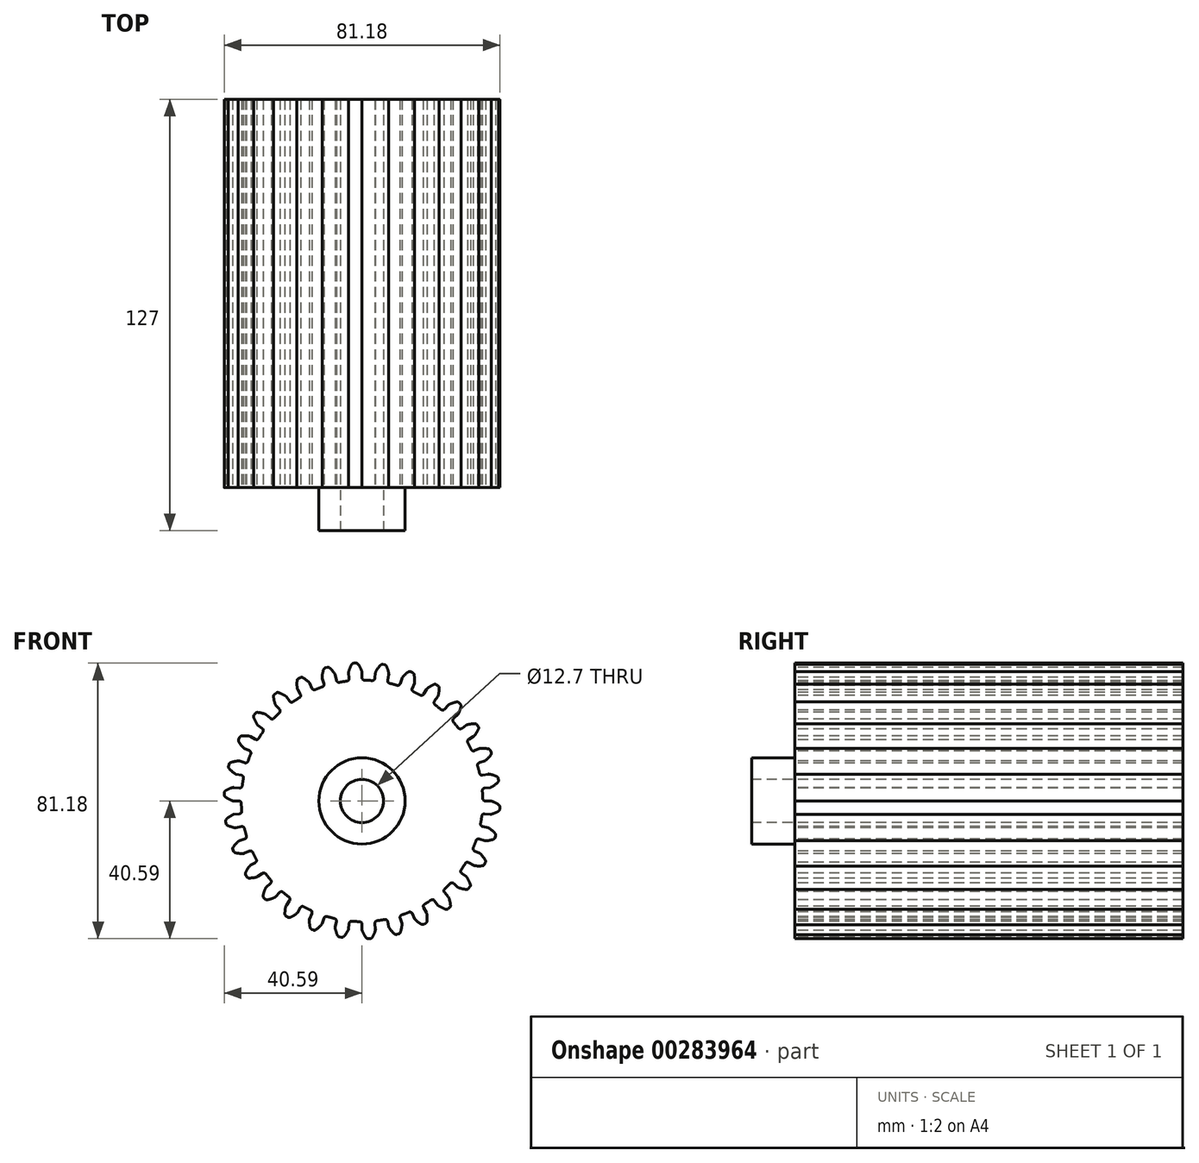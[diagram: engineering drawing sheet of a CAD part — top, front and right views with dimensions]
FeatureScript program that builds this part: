
annotation { "Feature Type Name" : "Feature", "Feature Type Description" : "" }
export const myFeature = defineFeature(function(context is Context, id is Id, definition is map)
    precondition{}
    {
        {
            var Q0;
            Q0=qCreatedBy(makeId("Front.planeOp"),FACE);
            var sketch = newSketch(context, id + "F0", { "sketchPlane" : qUnion([Q0])});
            skCircle(sketch, "E0", {"center": v(0, 0) * mm, "radius": 35.56 * mm});
            skSolve(sketch);
        }
        {
            var Q0;
            Q0 = qSketchRegion(id + "F0", true);
            extrude(context, id + "F1", {"entities" : qUnion([Q0]), "depth" : 57.15 * mm});
        }
        {
            var Q0;
            Q0=makeQuery(id+"F1.opExtrude","CAP_FACE",FACE,{"disambiguationData":[OSD([sQuery(id+"F0.wireOp",EDGE,"E0")])],"isStart":true});
            extrude(context, id + "F2", {"entities" : qUnion([Q0]), "operationType" : NewBodyOperationType.ADD, "depth" : 57.15 * mm});
        }
        {
            var Q0;
            Q0=makeQuery(id+"F1.opExtrude","CAP_FACE",FACE,{"disambiguationData":[OSD([sQuery(id+"F0.wireOp",EDGE,"E0")])],"isStart":false});
            var sketch = newSketch(context, id + "F3", { "sketchPlane" : qUnion([Q0])});
            skArc(sketch, "E1.trimOffspring", {"start": v(-0.06, 38.24) * mm, "mid": v(-0.56, 39.3) * mm, "end": v(-1.18, 40.28) * mm});
            skLineSegment(sketch, "E2", {"start": v(-1.84, 40.6) * mm, "end": v(-2.13, 40.58) * mm});
            skLineSegment(sketch, "E3", {"start": v(0, 37.96) * mm, "end": v(0, 36.31) * mm});
            skLineSegment(sketch, "E4.MirrorCS", {"start": v(-2.41, 40.56) * mm, "end": v(-2.13, 40.58) * mm});
            skArc(sketch, "E5.MirrorCS", {"start": v(-3.94, 38.04) * mm, "mid": v(-3.55, 39.14) * mm, "end": v(-3.03, 40.18) * mm});
            skPoint(sketch, "E6.visualSharp", {"position": v(-3.76, 35.36) * mm});
            skPoint(sketch, "E7.visualSharp", {"position": v(0, 35.56) * mm});
            skArc(sketch, "E7.filletArc", {"start": v(0, 36.31) * mm, "mid": v(0.22, 35.78) * mm, "end": v(0.75, 35.55) * mm});
            skArc(sketch, "E8", {"start": v(0.75, 35.55) * mm, "mid": v(-1.88, 35.51) * mm, "end": v(-4.5, 35.27) * mm});
            skLineSegment(sketch, "E9.MirrorCS", {"start": v(-3.97, 37.75) * mm, "end": v(-3.8, 36.12) * mm});
            skArc(sketch, "E10.MirrorCS", {"start": v(-3.8, 36.12) * mm, "mid": v(-3.96, 35.56) * mm, "end": v(-4.46, 35.28) * mm});
            skPoint(sketch, "E11.visualSharp", {"position": v(-3.98, 37.9) * mm});
            skArc(sketch, "E11.filletArc", {"start": v(-3.94, 38.04) * mm, "mid": v(-3.97, 37.9) * mm, "end": v(-3.97, 37.75) * mm});
            skPoint(sketch, "E12.visualSharp", {"position": v(-2.81, 40.54) * mm});
            skArc(sketch, "E12.filletArc", {"start": v(-2.41, 40.56) * mm, "mid": v(-2.77, 40.45) * mm, "end": v(-3.03, 40.18) * mm});
            skPoint(sketch, "E13.visualSharp", {"position": v(-1.44, 40.61) * mm});
            skArc(sketch, "E13.filletArc", {"start": v(-1.18, 40.28) * mm, "mid": v(-1.47, 40.52) * mm, "end": v(-1.84, 40.6) * mm});
            skPoint(sketch, "E14.visualSharp", {"position": v(0, 38.1) * mm});
            skArc(sketch, "E14.filletArc", {"start": v(0, 37.96) * mm, "mid": v(-0.01, 38.1) * mm, "end": v(-0.06, 38.24) * mm});
            skPoint(sketch, "E15.1.0", {"position": v(-11.77, 36.24) * mm});
            skArc(sketch, "E15.1.1", {"start": v(-6.66, 34.93) * mm, "mid": v(-9.22, 34.34) * mm, "end": v(-11.73, 33.57) * mm});
            skLineSegment(sketch, "E15.1.2", {"start": v(-11.73, 36.1) * mm, "end": v(-11.22, 34.54) * mm});
            skArc(sketch, "E15.1.3", {"start": v(-7.55, 35.52) * mm, "mid": v(-7.23, 35.04) * mm, "end": v(-6.66, 34.93) * mm});
            skPoint(sketch, "E15.1.4", {"position": v(-7.92, 37.27) * mm});
            skPoint(sketch, "E15.1.5", {"position": v(-7.4, 34.78) * mm});
            skArc(sketch, "E15.1.6", {"start": v(-11.22, 34.54) * mm, "mid": v(-11.26, 33.96) * mm, "end": v(-11.7, 33.58) * mm});
            skArc(sketch, "E15.1.7", {"start": v(-11.76, 36.39) * mm, "mid": v(-11.61, 37.54) * mm, "end": v(-11.32, 38.68) * mm});
            skPoint(sketch, "E15.1.8", {"position": v(-11.18, 39.07) * mm});
            skArc(sketch, "E15.1.9", {"start": v(-8, 37.4) * mm, "mid": v(-8.72, 38.32) * mm, "end": v(-9.53, 39.15) * mm});
            skPoint(sketch, "E15.1.10", {"position": v(-9.85, 39.43) * mm});
            skPoint(sketch, "E15.1.11", {"position": v(-11.03, 33.8) * mm});
            skLineSegment(sketch, "E15.1.12", {"start": v(-7.9, 37.13) * mm, "end": v(-7.55, 35.52) * mm});
            skArc(sketch, "E15.1.13", {"start": v(-9.53, 39.15) * mm, "mid": v(-9.87, 39.33) * mm, "end": v(-10.24, 39.32) * mm});
            skArc(sketch, "E15.1.14", {"start": v(-10.8, 39.18) * mm, "mid": v(-11.12, 39) * mm, "end": v(-11.32, 38.68) * mm});
            skLineSegment(sketch, "E15.1.15", {"start": v(-10.8, 39.18) * mm, "end": v(-10.52, 39.25) * mm});
            skLineSegment(sketch, "E15.1.16", {"start": v(-10.24, 39.32) * mm, "end": v(-10.52, 39.25) * mm});
            skArc(sketch, "E15.1.17", {"start": v(-11.76, 36.39) * mm, "mid": v(-11.76, 36.24) * mm, "end": v(-11.73, 36.1) * mm});
            skArc(sketch, "E15.1.18", {"start": v(-7.9, 37.13) * mm, "mid": v(-7.94, 37.27) * mm, "end": v(-8, 37.4) * mm});
            skPoint(sketch, "E15.2.0", {"position": v(-19.05, 33) * mm});
            skArc(sketch, "E15.2.1", {"start": v(-13.78, 32.78) * mm, "mid": v(-16.16, 31.67) * mm, "end": v(-18.46, 30.4) * mm});
            skLineSegment(sketch, "E15.2.2", {"start": v(-18.98, 32.87) * mm, "end": v(-18.16, 31.45) * mm});
            skArc(sketch, "E15.2.3", {"start": v(-14.77, 33.17) * mm, "mid": v(-14.35, 32.78) * mm, "end": v(-13.78, 32.78) * mm});
            skPoint(sketch, "E15.2.4", {"position": v(-15.5, 34.8) * mm});
            skPoint(sketch, "E15.2.5", {"position": v(-14.46, 32.49) * mm});
            skArc(sketch, "E15.2.6", {"start": v(-18.16, 31.45) * mm, "mid": v(-18.08, 30.88) * mm, "end": v(-18.42, 30.42) * mm});
            skArc(sketch, "E15.2.7", {"start": v(-19.07, 33.14) * mm, "mid": v(-19.16, 34.3) * mm, "end": v(-19.11, 35.48) * mm});
            skPoint(sketch, "E15.2.8", {"position": v(-19.06, 35.9) * mm});
            skArc(sketch, "E15.2.9", {"start": v(-15.6, 34.91) * mm, "mid": v(-16.5, 35.67) * mm, "end": v(-17.47, 36.32) * mm});
            skPoint(sketch, "E15.2.10", {"position": v(-17.83, 36.52) * mm});
            skPoint(sketch, "E15.2.11", {"position": v(-17.82, 30.77) * mm});
            skLineSegment(sketch, "E15.2.12", {"start": v(-15.44, 34.67) * mm, "end": v(-14.77, 33.17) * mm});
            skArc(sketch, "E15.2.13", {"start": v(-17.47, 36.32) * mm, "mid": v(-17.83, 36.42) * mm, "end": v(-18.2, 36.34) * mm});
            skArc(sketch, "E15.2.14", {"start": v(-18.7, 36.08) * mm, "mid": v(-18.98, 35.83) * mm, "end": v(-19.11, 35.48) * mm});
            skLineSegment(sketch, "E15.2.15", {"start": v(-18.7, 36.08) * mm, "end": v(-18.45, 36.2) * mm});
            skLineSegment(sketch, "E15.2.16", {"start": v(-18.2, 36.34) * mm, "end": v(-18.45, 36.2) * mm});
            skArc(sketch, "E15.2.17", {"start": v(-19.07, 33.14) * mm, "mid": v(-19.04, 33) * mm, "end": v(-18.98, 32.87) * mm});
            skArc(sketch, "E15.2.18", {"start": v(-15.44, 34.67) * mm, "mid": v(-15.5, 34.8) * mm, "end": v(-15.6, 34.91) * mm});
            skArc(sketch, "E16.1.3.0", {"start": v(-20.3, 29.2) * mm, "mid": v(-22.4, 27.62) * mm, "end": v(-24.37, 25.9) * mm});
            skLineSegment(sketch, "E16.5.3.0", {"start": v(-25.4, 28.2) * mm, "end": v(-24.3, 26.99) * mm});
            skArc(sketch, "E16.8.3.0", {"start": v(-21.34, 29.38) * mm, "mid": v(-20.86, 29.08) * mm, "end": v(-20.3, 29.2) * mm});
            skPoint(sketch, "E16.12.3.0", {"position": v(-22.4, 30.82) * mm});
            skPoint(sketch, "E16.13.3.0", {"position": v(-20.9, 28.77) * mm});
            skArc(sketch, "E16.14.3.0", {"start": v(-24.3, 26.99) * mm, "mid": v(-24.1, 26.44) * mm, "end": v(-24.34, 25.92) * mm});
            skArc(sketch, "E16.18.3.0", {"start": v(-25.55, 28.45) * mm, "mid": v(-25.88, 29.57) * mm, "end": v(-26.07, 30.73) * mm});
            skPoint(sketch, "E16.22.3.0", {"position": v(-26.1, 31.15) * mm});
            skArc(sketch, "E16.23.3.0", {"start": v(-22.52, 30.9) * mm, "mid": v(-23.55, 31.46) * mm, "end": v(-24.63, 31.9) * mm});
            skPoint(sketch, "E16.24.3.0", {"position": v(-25.5, 28.31) * mm});
            skPoint(sketch, "E16.27.3.0", {"position": v(-25.04, 32.01) * mm});
            skPoint(sketch, "E16.28.3.0", {"position": v(-23.83, 26.4) * mm});
            skLineSegment(sketch, "E16.29.3.0", {"start": v(-22.3, 30.7) * mm, "end": v(-21.34, 29.38) * mm});
            skArc(sketch, "E16.32.3.0", {"start": v(-24.63, 31.9) * mm, "mid": v(-25, 31.92) * mm, "end": v(-25.35, 31.76) * mm});
            skArc(sketch, "E16.36.3.0", {"start": v(-25.8, 31.4) * mm, "mid": v(-26.02, 31.1) * mm, "end": v(-26.07, 30.73) * mm});
            skLineSegment(sketch, "E16.40.3.0", {"start": v(-25.8, 31.4) * mm, "end": v(-25.57, 31.58) * mm});
            skLineSegment(sketch, "E16.43.3.0", {"start": v(-25.35, 31.76) * mm, "end": v(-25.57, 31.58) * mm});
            skArc(sketch, "E16.46.3.0", {"start": v(-25.55, 28.45) * mm, "mid": v(-25.48, 28.32) * mm, "end": v(-25.4, 28.2) * mm});
            skArc(sketch, "E16.50.3.0", {"start": v(-22.3, 30.7) * mm, "mid": v(-22.4, 30.82) * mm, "end": v(-22.52, 30.9) * mm});
            skArc(sketch, "E16.1.4.0", {"start": v(-25.92, 24.34) * mm, "mid": v(-27.65, 22.36) * mm, "end": v(-29.22, 20.26) * mm});
            skLineSegment(sketch, "E16.5.4.0", {"start": v(-30.7, 22.3) * mm, "end": v(-29.38, 21.34) * mm});
            skArc(sketch, "E16.8.4.0", {"start": v(-26.99, 24.3) * mm, "mid": v(-26.44, 24.1) * mm, "end": v(-25.92, 24.34) * mm});
            skPoint(sketch, "E16.12.4.0", {"position": v(-28.31, 25.5) * mm});
            skPoint(sketch, "E16.13.4.0", {"position": v(-26.43, 23.8) * mm});
            skArc(sketch, "E16.14.4.0", {"start": v(-29.38, 21.34) * mm, "mid": v(-29.08, 20.86) * mm, "end": v(-29.2, 20.3) * mm});
            skArc(sketch, "E16.18.4.0", {"start": v(-30.9, 22.52) * mm, "mid": v(-31.46, 23.55) * mm, "end": v(-31.9, 24.63) * mm});
            skPoint(sketch, "E16.22.4.0", {"position": v(-32.01, 25.04) * mm});
            skArc(sketch, "E16.23.4.0", {"start": v(-28.45, 25.55) * mm, "mid": v(-29.57, 25.88) * mm, "end": v(-30.73, 26.07) * mm});
            skPoint(sketch, "E16.24.4.0", {"position": v(-30.82, 22.4) * mm});
            skPoint(sketch, "E16.27.4.0", {"position": v(-31.15, 26.1) * mm});
            skPoint(sketch, "E16.28.4.0", {"position": v(-28.8, 20.87) * mm});
            skLineSegment(sketch, "E16.29.4.0", {"start": v(-28.2, 25.4) * mm, "end": v(-26.99, 24.3) * mm});
            skArc(sketch, "E16.32.4.0", {"start": v(-30.73, 26.07) * mm, "mid": v(-31.1, 26.02) * mm, "end": v(-31.4, 25.8) * mm});
            skArc(sketch, "E16.36.4.0", {"start": v(-31.76, 25.35) * mm, "mid": v(-31.92, 25) * mm, "end": v(-31.9, 24.63) * mm});
            skLineSegment(sketch, "E16.40.4.0", {"start": v(-31.76, 25.35) * mm, "end": v(-31.58, 25.57) * mm});
            skLineSegment(sketch, "E16.43.4.0", {"start": v(-31.4, 25.8) * mm, "end": v(-31.58, 25.57) * mm});
            skArc(sketch, "E16.46.4.0", {"start": v(-30.9, 22.52) * mm, "mid": v(-30.82, 22.4) * mm, "end": v(-30.7, 22.3) * mm});
            skArc(sketch, "E16.50.4.0", {"start": v(-28.2, 25.4) * mm, "mid": v(-28.32, 25.48) * mm, "end": v(-28.45, 25.55) * mm});
            skArc(sketch, "E16.1.5.0", {"start": v(-30.42, 18.42) * mm, "mid": v(-31.7, 16.13) * mm, "end": v(-32.8, 13.74) * mm});
            skLineSegment(sketch, "E16.5.5.0", {"start": v(-34.67, 15.44) * mm, "end": v(-33.17, 14.77) * mm});
            skArc(sketch, "E16.8.5.0", {"start": v(-31.45, 18.16) * mm, "mid": v(-30.88, 18.08) * mm, "end": v(-30.42, 18.42) * mm});
            skPoint(sketch, "E16.12.5.0", {"position": v(-33, 19.05) * mm});
            skPoint(sketch, "E16.13.5.0", {"position": v(-30.8, 17.78) * mm});
            skArc(sketch, "E16.14.5.0", {"start": v(-33.17, 14.77) * mm, "mid": v(-32.78, 14.35) * mm, "end": v(-32.78, 13.78) * mm});
            skArc(sketch, "E16.18.5.0", {"start": v(-34.91, 15.6) * mm, "mid": v(-35.67, 16.5) * mm, "end": v(-36.32, 17.47) * mm});
            skPoint(sketch, "E16.22.5.0", {"position": v(-36.52, 17.83) * mm});
            skArc(sketch, "E16.23.5.0", {"start": v(-33.14, 19.07) * mm, "mid": v(-34.3, 19.16) * mm, "end": v(-35.48, 19.11) * mm});
            skPoint(sketch, "E16.24.5.0", {"position": v(-34.8, 15.5) * mm});
            skPoint(sketch, "E16.27.5.0", {"position": v(-35.9, 19.06) * mm});
            skPoint(sketch, "E16.28.5.0", {"position": v(-32.5, 14.42) * mm});
            skLineSegment(sketch, "E16.29.5.0", {"start": v(-32.87, 18.98) * mm, "end": v(-31.45, 18.16) * mm});
            skArc(sketch, "E16.32.5.0", {"start": v(-35.48, 19.11) * mm, "mid": v(-35.83, 18.98) * mm, "end": v(-36.08, 18.7) * mm});
            skArc(sketch, "E16.36.5.0", {"start": v(-36.34, 18.2) * mm, "mid": v(-36.42, 17.83) * mm, "end": v(-36.32, 17.47) * mm});
            skLineSegment(sketch, "E16.40.5.0", {"start": v(-36.34, 18.2) * mm, "end": v(-36.2, 18.45) * mm});
            skLineSegment(sketch, "E16.43.5.0", {"start": v(-36.08, 18.7) * mm, "end": v(-36.2, 18.45) * mm});
            skArc(sketch, "E16.46.5.0", {"start": v(-34.91, 15.6) * mm, "mid": v(-34.8, 15.5) * mm, "end": v(-34.67, 15.44) * mm});
            skArc(sketch, "E16.50.5.0", {"start": v(-32.87, 18.98) * mm, "mid": v(-33, 19.04) * mm, "end": v(-33.14, 19.07) * mm});
            skArc(sketch, "E16.1.6.0", {"start": v(-33.58, 11.7) * mm, "mid": v(-34.35, 9.18) * mm, "end": v(-34.94, 6.62) * mm});
            skLineSegment(sketch, "E16.5.6.0", {"start": v(-37.13, 7.9) * mm, "end": v(-35.52, 7.55) * mm});
            skArc(sketch, "E16.8.6.0", {"start": v(-34.54, 11.22) * mm, "mid": v(-33.96, 11.26) * mm, "end": v(-33.58, 11.7) * mm});
            skPoint(sketch, "E16.12.6.0", {"position": v(-36.24, 11.77) * mm});
            skPoint(sketch, "E16.13.6.0", {"position": v(-33.82, 10.99) * mm});
            skArc(sketch, "E16.14.6.0", {"start": v(-35.52, 7.55) * mm, "mid": v(-35.04, 7.23) * mm, "end": v(-34.93, 6.66) * mm});
            skArc(sketch, "E16.18.6.0", {"start": v(-37.4, 8) * mm, "mid": v(-38.32, 8.72) * mm, "end": v(-39.15, 9.53) * mm});
            skPoint(sketch, "E16.22.6.0", {"position": v(-39.43, 9.85) * mm});
            skArc(sketch, "E16.23.6.0", {"start": v(-36.39, 11.76) * mm, "mid": v(-37.54, 11.61) * mm, "end": v(-38.68, 11.32) * mm});
            skPoint(sketch, "E16.24.6.0", {"position": v(-37.27, 7.92) * mm});
            skPoint(sketch, "E16.27.6.0", {"position": v(-39.07, 11.18) * mm});
            skPoint(sketch, "E16.28.6.0", {"position": v(-34.8, 7.35) * mm});
            skLineSegment(sketch, "E16.29.6.0", {"start": v(-36.1, 11.73) * mm, "end": v(-34.54, 11.22) * mm});
            skArc(sketch, "E16.32.6.0", {"start": v(-38.68, 11.32) * mm, "mid": v(-39, 11.12) * mm, "end": v(-39.18, 10.8) * mm});
            skArc(sketch, "E16.36.6.0", {"start": v(-39.32, 10.24) * mm, "mid": v(-39.33, 9.87) * mm, "end": v(-39.15, 9.53) * mm});
            skLineSegment(sketch, "E16.40.6.0", {"start": v(-39.32, 10.24) * mm, "end": v(-39.25, 10.52) * mm});
            skLineSegment(sketch, "E16.43.6.0", {"start": v(-39.18, 10.8) * mm, "end": v(-39.25, 10.52) * mm});
            skArc(sketch, "E16.46.6.0", {"start": v(-37.4, 8) * mm, "mid": v(-37.27, 7.94) * mm, "end": v(-37.13, 7.9) * mm});
            skArc(sketch, "E16.50.6.0", {"start": v(-36.1, 11.73) * mm, "mid": v(-36.24, 11.76) * mm, "end": v(-36.39, 11.76) * mm});
            skArc(sketch, "E16.1.7.0", {"start": v(-35.28, 4.46) * mm, "mid": v(-35.51, 1.84) * mm, "end": v(-35.55, -0.79) * mm});
            skLineSegment(sketch, "E16.5.7.0", {"start": v(-37.96, 0) * mm, "end": v(-36.31, 0) * mm});
            skArc(sketch, "E16.8.7.0", {"start": v(-36.12, 3.8) * mm, "mid": v(-35.56, 3.96) * mm, "end": v(-35.28, 4.46) * mm});
            skPoint(sketch, "E16.12.7.0", {"position": v(-37.9, 3.98) * mm});
            skPoint(sketch, "E16.13.7.0", {"position": v(-35.37, 3.72) * mm});
            skArc(sketch, "E16.14.7.0", {"start": v(-36.31, 0) * mm, "mid": v(-35.78, -0.22) * mm, "end": v(-35.55, -0.75) * mm});
            skArc(sketch, "E16.18.7.0", {"start": v(-38.24, 0.06) * mm, "mid": v(-39.3, 0.56) * mm, "end": v(-40.28, 1.18) * mm});
            skPoint(sketch, "E16.22.7.0", {"position": v(-40.61, 1.44) * mm});
            skArc(sketch, "E16.23.7.0", {"start": v(-38.04, 3.94) * mm, "mid": v(-39.14, 3.55) * mm, "end": v(-40.18, 3.03) * mm});
            skPoint(sketch, "E16.24.7.0", {"position": v(-38.1, 0) * mm});
            skPoint(sketch, "E16.27.7.0", {"position": v(-40.54, 2.81) * mm});
            skPoint(sketch, "E16.28.7.0", {"position": v(-35.56, -0.04) * mm});
            skLineSegment(sketch, "E16.29.7.0", {"start": v(-37.75, 3.97) * mm, "end": v(-36.12, 3.8) * mm});
            skArc(sketch, "E16.32.7.0", {"start": v(-40.18, 3.03) * mm, "mid": v(-40.45, 2.77) * mm, "end": v(-40.56, 2.41) * mm});
            skArc(sketch, "E16.36.7.0", {"start": v(-40.6, 1.84) * mm, "mid": v(-40.52, 1.47) * mm, "end": v(-40.28, 1.18) * mm});
            skLineSegment(sketch, "E16.40.7.0", {"start": v(-40.6, 1.84) * mm, "end": v(-40.58, 2.13) * mm});
            skLineSegment(sketch, "E16.43.7.0", {"start": v(-40.56, 2.41) * mm, "end": v(-40.58, 2.13) * mm});
            skArc(sketch, "E16.46.7.0", {"start": v(-38.24, 0.06) * mm, "mid": v(-38.1, 0.01) * mm, "end": v(-37.96, 0) * mm});
            skArc(sketch, "E16.50.7.0", {"start": v(-37.75, 3.97) * mm, "mid": v(-37.9, 3.97) * mm, "end": v(-38.04, 3.94) * mm});
            skArc(sketch, "E16.1.8.0", {"start": v(-35.44, -2.97) * mm, "mid": v(-35.12, -5.58) * mm, "end": v(-34.61, -8.16) * mm});
            skLineSegment(sketch, "E16.5.8.0", {"start": v(-37.13, -7.9) * mm, "end": v(-35.52, -7.55) * mm});
            skArc(sketch, "E16.8.8.0", {"start": v(-36.12, -3.8) * mm, "mid": v(-35.6, -3.52) * mm, "end": v(-35.44, -2.97) * mm});
            skPoint(sketch, "E16.12.8.0", {"position": v(-37.9, -3.98) * mm});
            skPoint(sketch, "E16.13.8.0", {"position": v(-35.37, -3.72) * mm});
            skArc(sketch, "E16.14.8.0", {"start": v(-35.52, -7.55) * mm, "mid": v(-34.95, -7.65) * mm, "end": v(-34.62, -8.12) * mm});
            skArc(sketch, "E16.18.8.0", {"start": v(-37.42, -7.9) * mm, "mid": v(-38.55, -7.62) * mm, "end": v(-39.65, -7.22) * mm});
            skPoint(sketch, "E16.22.8.0", {"position": v(-40.03, -7.04) * mm});
            skArc(sketch, "E16.23.8.0", {"start": v(-38.02, -4.05) * mm, "mid": v(-39.02, -4.66) * mm, "end": v(-39.94, -5.39) * mm});
            skPoint(sketch, "E16.24.8.0", {"position": v(-37.27, -7.92) * mm});
            skPoint(sketch, "E16.27.8.0", {"position": v(-40.24, -5.68) * mm});
            skPoint(sketch, "E16.28.8.0", {"position": v(-34.77, -7.43) * mm});
            skLineSegment(sketch, "E16.29.8.0", {"start": v(-37.75, -3.97) * mm, "end": v(-36.12, -3.8) * mm});
            skArc(sketch, "E16.32.8.0", {"start": v(-39.94, -5.39) * mm, "mid": v(-40.14, -5.7) * mm, "end": v(-40.18, -6.07) * mm});
            skArc(sketch, "E16.36.8.0", {"start": v(-40.09, -6.64) * mm, "mid": v(-39.94, -6.98) * mm, "end": v(-39.65, -7.22) * mm});
            skLineSegment(sketch, "E16.40.8.0", {"start": v(-40.09, -6.64) * mm, "end": v(-40.13, -6.36) * mm});
            skLineSegment(sketch, "E16.43.8.0", {"start": v(-40.18, -6.07) * mm, "end": v(-40.13, -6.36) * mm});
            skArc(sketch, "E16.46.8.0", {"start": v(-37.42, -7.9) * mm, "mid": v(-37.27, -7.9) * mm, "end": v(-37.13, -7.9) * mm});
            skArc(sketch, "E16.50.8.0", {"start": v(-37.75, -3.97) * mm, "mid": v(-37.9, -4) * mm, "end": v(-38.02, -4.05) * mm});
            skArc(sketch, "E16.1.9.0", {"start": v(-34.04, -10.28) * mm, "mid": v(-33.2, -12.76) * mm, "end": v(-32.16, -15.18) * mm});
            skLineSegment(sketch, "E16.5.9.0", {"start": v(-34.67, -15.44) * mm, "end": v(-33.17, -14.77) * mm});
            skArc(sketch, "E16.8.9.0", {"start": v(-34.54, -11.22) * mm, "mid": v(-34.1, -10.85) * mm, "end": v(-34.04, -10.28) * mm});
            skPoint(sketch, "E16.12.9.0", {"position": v(-36.24, -11.77) * mm});
            skPoint(sketch, "E16.13.9.0", {"position": v(-33.82, -10.99) * mm});
            skArc(sketch, "E16.14.9.0", {"start": v(-33.17, -14.77) * mm, "mid": v(-32.6, -14.75) * mm, "end": v(-32.18, -15.14) * mm});
            skArc(sketch, "E16.18.9.0", {"start": v(-34.96, -15.5) * mm, "mid": v(-36.12, -15.47) * mm, "end": v(-37.28, -15.3) * mm});
            skPoint(sketch, "E16.22.9.0", {"position": v(-37.69, -15.2) * mm});
            skArc(sketch, "E16.23.9.0", {"start": v(-36.35, -11.87) * mm, "mid": v(-37.2, -12.67) * mm, "end": v(-37.94, -13.57) * mm});
            skPoint(sketch, "E16.24.9.0", {"position": v(-34.8, -15.5) * mm});
            skPoint(sketch, "E16.27.9.0", {"position": v(-38.18, -13.92) * mm});
            skPoint(sketch, "E16.28.9.0", {"position": v(-32.47, -14.5) * mm});
            skLineSegment(sketch, "E16.29.9.0", {"start": v(-36.1, -11.73) * mm, "end": v(-34.54, -11.22) * mm});
            skArc(sketch, "E16.32.9.0", {"start": v(-37.94, -13.57) * mm, "mid": v(-38.08, -13.92) * mm, "end": v(-38.04, -14.3) * mm});
            skArc(sketch, "E16.36.9.0", {"start": v(-37.83, -14.83) * mm, "mid": v(-37.62, -15.14) * mm, "end": v(-37.28, -15.3) * mm});
            skLineSegment(sketch, "E16.40.9.0", {"start": v(-37.83, -14.83) * mm, "end": v(-37.94, -14.56) * mm});
            skLineSegment(sketch, "E16.43.9.0", {"start": v(-38.04, -14.3) * mm, "end": v(-37.94, -14.56) * mm});
            skArc(sketch, "E16.46.9.0", {"start": v(-34.96, -15.5) * mm, "mid": v(-34.81, -15.48) * mm, "end": v(-34.67, -15.44) * mm});
            skArc(sketch, "E16.50.9.0", {"start": v(-36.1, -11.73) * mm, "mid": v(-36.23, -11.79) * mm, "end": v(-36.35, -11.87) * mm});
            skArc(sketch, "E16.1.10.0", {"start": v(-31.16, -17.13) * mm, "mid": v(-29.81, -19.38) * mm, "end": v(-28.3, -21.53) * mm});
            skLineSegment(sketch, "E16.5.10.0", {"start": v(-30.7, -22.3) * mm, "end": v(-29.38, -21.34) * mm});
            skArc(sketch, "E16.8.10.0", {"start": v(-31.45, -18.16) * mm, "mid": v(-31.1, -17.7) * mm, "end": v(-31.16, -17.13) * mm});
            skPoint(sketch, "E16.12.10.0", {"position": v(-33, -19.05) * mm});
            skPoint(sketch, "E16.13.10.0", {"position": v(-30.8, -17.78) * mm});
            skArc(sketch, "E16.14.10.0", {"start": v(-29.38, -21.34) * mm, "mid": v(-28.82, -21.2) * mm, "end": v(-28.32, -21.5) * mm});
            skArc(sketch, "E16.18.10.0", {"start": v(-30.97, -22.43) * mm, "mid": v(-32.12, -22.65) * mm, "end": v(-33.28, -22.72) * mm});
            skPoint(sketch, "E16.22.10.0", {"position": v(-33.7, -22.7) * mm});
            skArc(sketch, "E16.23.10.0", {"start": v(-33.09, -19.17) * mm, "mid": v(-33.75, -20.13) * mm, "end": v(-34.3, -21.17) * mm});
            skPoint(sketch, "E16.24.10.0", {"position": v(-30.82, -22.4) * mm});
            skPoint(sketch, "E16.27.10.0", {"position": v(-34.45, -21.55) * mm});
            skPoint(sketch, "E16.28.10.0", {"position": v(-28.74, -20.94) * mm});
            skLineSegment(sketch, "E16.29.10.0", {"start": v(-32.87, -18.98) * mm, "end": v(-31.45, -18.16) * mm});
            skArc(sketch, "E16.32.10.0", {"start": v(-34.3, -21.17) * mm, "mid": v(-34.35, -21.54) * mm, "end": v(-34.23, -21.9) * mm});
            skArc(sketch, "E16.36.10.0", {"start": v(-33.92, -22.37) * mm, "mid": v(-33.65, -22.63) * mm, "end": v(-33.28, -22.72) * mm});
            skLineSegment(sketch, "E16.40.10.0", {"start": v(-33.92, -22.37) * mm, "end": v(-34.08, -22.13) * mm});
            skLineSegment(sketch, "E16.43.10.0", {"start": v(-34.23, -21.9) * mm, "end": v(-34.08, -22.13) * mm});
            skArc(sketch, "E16.46.10.0", {"start": v(-30.97, -22.43) * mm, "mid": v(-30.83, -22.38) * mm, "end": v(-30.7, -22.3) * mm});
            skArc(sketch, "E16.50.10.0", {"start": v(-32.87, -18.98) * mm, "mid": v(-32.99, -19.06) * mm, "end": v(-33.09, -19.17) * mm});
            skArc(sketch, "E16.1.11.0", {"start": v(-26.92, -23.23) * mm, "mid": v(-25.13, -25.16) * mm, "end": v(-23.2, -26.95) * mm});
            skLineSegment(sketch, "E16.5.11.0", {"start": v(-25.4, -28.2) * mm, "end": v(-24.3, -26.99) * mm});
            skArc(sketch, "E16.8.11.0", {"start": v(-26.99, -24.3) * mm, "mid": v(-26.74, -23.78) * mm, "end": v(-26.92, -23.23) * mm});
            skPoint(sketch, "E16.12.11.0", {"position": v(-28.31, -25.5) * mm});
            skPoint(sketch, "E16.13.11.0", {"position": v(-26.43, -23.8) * mm});
            skArc(sketch, "E16.14.11.0", {"start": v(-24.3, -26.99) * mm, "mid": v(-23.78, -26.74) * mm, "end": v(-23.23, -26.92) * mm});
            skArc(sketch, "E16.18.11.0", {"start": v(-25.63, -28.38) * mm, "mid": v(-26.7, -28.83) * mm, "end": v(-27.83, -29.14) * mm});
            skPoint(sketch, "E16.22.11.0", {"position": v(-28.25, -29.22) * mm});
            skArc(sketch, "E16.23.11.0", {"start": v(-28.38, -25.63) * mm, "mid": v(-28.83, -26.7) * mm, "end": v(-29.14, -27.83) * mm});
            skPoint(sketch, "E16.24.11.0", {"position": v(-25.5, -28.31) * mm});
            skPoint(sketch, "E16.27.11.0", {"position": v(-29.22, -28.25) * mm});
            skPoint(sketch, "E16.28.11.0", {"position": v(-23.76, -26.45) * mm});
            skLineSegment(sketch, "E16.29.11.0", {"start": v(-28.2, -25.4) * mm, "end": v(-26.99, -24.3) * mm});
            skArc(sketch, "E16.32.11.0", {"start": v(-29.14, -27.83) * mm, "mid": v(-29.13, -28.2) * mm, "end": v(-28.93, -28.53) * mm});
            skArc(sketch, "E16.36.11.0", {"start": v(-28.53, -28.93) * mm, "mid": v(-28.2, -29.13) * mm, "end": v(-27.83, -29.14) * mm});
            skLineSegment(sketch, "E16.40.11.0", {"start": v(-28.53, -28.93) * mm, "end": v(-28.73, -28.73) * mm});
            skLineSegment(sketch, "E16.43.11.0", {"start": v(-28.93, -28.53) * mm, "end": v(-28.73, -28.73) * mm});
            skArc(sketch, "E16.46.11.0", {"start": v(-25.63, -28.38) * mm, "mid": v(-25.5, -28.3) * mm, "end": v(-25.4, -28.2) * mm});
            skArc(sketch, "E16.50.11.0", {"start": v(-28.2, -25.4) * mm, "mid": v(-28.3, -25.5) * mm, "end": v(-28.38, -25.63) * mm});
            skArc(sketch, "E16.1.12.0", {"start": v(-21.5, -28.32) * mm, "mid": v(-19.35, -29.83) * mm, "end": v(-17.1, -31.18) * mm});
            skLineSegment(sketch, "E16.5.12.0", {"start": v(-18.98, -32.87) * mm, "end": v(-18.16, -31.45) * mm});
            skArc(sketch, "E16.8.12.0", {"start": v(-21.34, -29.38) * mm, "mid": v(-21.2, -28.82) * mm, "end": v(-21.5, -28.32) * mm});
            skPoint(sketch, "E16.12.12.0", {"position": v(-22.4, -30.82) * mm});
            skPoint(sketch, "E16.13.12.0", {"position": v(-20.9, -28.77) * mm});
            skArc(sketch, "E16.14.12.0", {"start": v(-18.16, -31.45) * mm, "mid": v(-17.7, -31.1) * mm, "end": v(-17.13, -31.16) * mm});
            skArc(sketch, "E16.18.12.0", {"start": v(-19.17, -33.09) * mm, "mid": v(-20.13, -33.75) * mm, "end": v(-21.17, -34.3) * mm});
            skPoint(sketch, "E16.22.12.0", {"position": v(-21.55, -34.45) * mm});
            skArc(sketch, "E16.23.12.0", {"start": v(-22.43, -30.97) * mm, "mid": v(-22.65, -32.12) * mm, "end": v(-22.72, -33.28) * mm});
            skPoint(sketch, "E16.24.12.0", {"position": v(-19.05, -33) * mm});
            skPoint(sketch, "E16.27.12.0", {"position": v(-22.7, -33.7) * mm});
            skPoint(sketch, "E16.28.12.0", {"position": v(-17.74, -30.82) * mm});
            skLineSegment(sketch, "E16.29.12.0", {"start": v(-22.3, -30.7) * mm, "end": v(-21.34, -29.38) * mm});
            skArc(sketch, "E16.32.12.0", {"start": v(-22.72, -33.28) * mm, "mid": v(-22.63, -33.65) * mm, "end": v(-22.37, -33.92) * mm});
            skArc(sketch, "E16.36.12.0", {"start": v(-21.9, -34.23) * mm, "mid": v(-21.54, -34.35) * mm, "end": v(-21.17, -34.3) * mm});
            skLineSegment(sketch, "E16.40.12.0", {"start": v(-21.9, -34.23) * mm, "end": v(-22.13, -34.08) * mm});
            skLineSegment(sketch, "E16.43.12.0", {"start": v(-22.37, -33.92) * mm, "end": v(-22.13, -34.08) * mm});
            skArc(sketch, "E16.46.12.0", {"start": v(-19.17, -33.09) * mm, "mid": v(-19.06, -32.99) * mm, "end": v(-18.98, -32.87) * mm});
            skArc(sketch, "E16.50.12.0", {"start": v(-22.3, -30.7) * mm, "mid": v(-22.38, -30.83) * mm, "end": v(-22.43, -30.97) * mm});
            skArc(sketch, "E16.1.13.0", {"start": v(-15.14, -32.18) * mm, "mid": v(-12.72, -33.2) * mm, "end": v(-10.24, -34.05) * mm});
            skLineSegment(sketch, "E16.5.13.0", {"start": v(-11.73, -36.1) * mm, "end": v(-11.22, -34.54) * mm});
            skArc(sketch, "E16.8.13.0", {"start": v(-14.77, -33.17) * mm, "mid": v(-14.75, -32.6) * mm, "end": v(-15.14, -32.18) * mm});
            skPoint(sketch, "E16.12.13.0", {"position": v(-15.5, -34.8) * mm});
            skPoint(sketch, "E16.13.13.0", {"position": v(-14.46, -32.49) * mm});
            skArc(sketch, "E16.14.13.0", {"start": v(-11.22, -34.54) * mm, "mid": v(-10.85, -34.1) * mm, "end": v(-10.28, -34.04) * mm});
            skArc(sketch, "E16.18.13.0", {"start": v(-11.87, -36.35) * mm, "mid": v(-12.67, -37.2) * mm, "end": v(-13.57, -37.94) * mm});
            skPoint(sketch, "E16.22.13.0", {"position": v(-13.92, -38.18) * mm});
            skArc(sketch, "E16.23.13.0", {"start": v(-15.5, -34.96) * mm, "mid": v(-15.47, -36.12) * mm, "end": v(-15.3, -37.28) * mm});
            skPoint(sketch, "E16.24.13.0", {"position": v(-11.77, -36.24) * mm});
            skPoint(sketch, "E16.27.13.0", {"position": v(-15.2, -37.69) * mm});
            skPoint(sketch, "E16.28.13.0", {"position": v(-10.95, -33.83) * mm});
            skLineSegment(sketch, "E16.29.13.0", {"start": v(-15.44, -34.67) * mm, "end": v(-14.77, -33.17) * mm});
            skArc(sketch, "E16.32.13.0", {"start": v(-15.3, -37.28) * mm, "mid": v(-15.14, -37.62) * mm, "end": v(-14.83, -37.83) * mm});
            skArc(sketch, "E16.36.13.0", {"start": v(-14.3, -38.04) * mm, "mid": v(-13.92, -38.08) * mm, "end": v(-13.57, -37.94) * mm});
            skLineSegment(sketch, "E16.40.13.0", {"start": v(-14.3, -38.04) * mm, "end": v(-14.56, -37.94) * mm});
            skLineSegment(sketch, "E16.43.13.0", {"start": v(-14.83, -37.83) * mm, "end": v(-14.56, -37.94) * mm});
            skArc(sketch, "E16.46.13.0", {"start": v(-11.87, -36.35) * mm, "mid": v(-11.79, -36.23) * mm, "end": v(-11.73, -36.1) * mm});
            skArc(sketch, "E16.50.13.0", {"start": v(-15.44, -34.67) * mm, "mid": v(-15.48, -34.81) * mm, "end": v(-15.5, -34.96) * mm});
            skArc(sketch, "E16.1.14.0", {"start": v(-8.12, -34.62) * mm, "mid": v(-5.54, -35.13) * mm, "end": v(-2.93, -35.44) * mm});
            skLineSegment(sketch, "E16.5.14.0", {"start": v(-3.97, -37.75) * mm, "end": v(-3.8, -36.12) * mm});
            skArc(sketch, "E16.8.14.0", {"start": v(-7.55, -35.52) * mm, "mid": v(-7.65, -34.95) * mm, "end": v(-8.12, -34.62) * mm});
            skPoint(sketch, "E16.12.14.0", {"position": v(-7.92, -37.27) * mm});
            skPoint(sketch, "E16.13.14.0", {"position": v(-7.4, -34.78) * mm});
            skArc(sketch, "E16.14.14.0", {"start": v(-3.8, -36.12) * mm, "mid": v(-3.52, -35.6) * mm, "end": v(-2.97, -35.44) * mm});
            skArc(sketch, "E16.18.14.0", {"start": v(-4.05, -38.02) * mm, "mid": v(-4.66, -39.02) * mm, "end": v(-5.39, -39.94) * mm});
            skPoint(sketch, "E16.22.14.0", {"position": v(-5.68, -40.24) * mm});
            skArc(sketch, "E16.23.14.0", {"start": v(-7.9, -37.42) * mm, "mid": v(-7.62, -38.55) * mm, "end": v(-7.22, -39.65) * mm});
            skPoint(sketch, "E16.24.14.0", {"position": v(-3.98, -37.9) * mm});
            skPoint(sketch, "E16.27.14.0", {"position": v(-7.04, -40.03) * mm});
            skPoint(sketch, "E16.28.14.0", {"position": v(-3.67, -35.37) * mm});
            skLineSegment(sketch, "E16.29.14.0", {"start": v(-7.9, -37.13) * mm, "end": v(-7.55, -35.52) * mm});
            skArc(sketch, "E16.32.14.0", {"start": v(-7.22, -39.65) * mm, "mid": v(-6.98, -39.94) * mm, "end": v(-6.64, -40.09) * mm});
            skArc(sketch, "E16.36.14.0", {"start": v(-6.07, -40.18) * mm, "mid": v(-5.7, -40.14) * mm, "end": v(-5.39, -39.94) * mm});
            skLineSegment(sketch, "E16.40.14.0", {"start": v(-6.07, -40.18) * mm, "end": v(-6.36, -40.13) * mm});
            skLineSegment(sketch, "E16.43.14.0", {"start": v(-6.64, -40.09) * mm, "end": v(-6.36, -40.13) * mm});
            skArc(sketch, "E16.46.14.0", {"start": v(-4.05, -38.02) * mm, "mid": v(-4, -37.9) * mm, "end": v(-3.97, -37.75) * mm});
            skArc(sketch, "E16.50.14.0", {"start": v(-7.9, -37.13) * mm, "mid": v(-7.9, -37.27) * mm, "end": v(-7.9, -37.42) * mm});
            skArc(sketch, "E16.1.15.0", {"start": v(-0.75, -35.55) * mm, "mid": v(1.88, -35.51) * mm, "end": v(4.5, -35.27) * mm});
            skLineSegment(sketch, "E16.5.15.0", {"start": v(3.97, -37.75) * mm, "end": v(3.8, -36.12) * mm});
            skArc(sketch, "E16.8.15.0", {"start": v(0, -36.31) * mm, "mid": v(-0.22, -35.78) * mm, "end": v(-0.75, -35.55) * mm});
            skPoint(sketch, "E16.12.15.0", {"position": v(0, -38.1) * mm});
            skPoint(sketch, "E16.13.15.0", {"position": v(0, -35.56) * mm});
            skArc(sketch, "E16.14.15.0", {"start": v(3.8, -36.12) * mm, "mid": v(3.96, -35.56) * mm, "end": v(4.46, -35.28) * mm});
            skArc(sketch, "E16.18.15.0", {"start": v(3.94, -38.04) * mm, "mid": v(3.55, -39.14) * mm, "end": v(3.03, -40.18) * mm});
            skPoint(sketch, "E16.22.15.0", {"position": v(2.81, -40.54) * mm});
            skArc(sketch, "E16.23.15.0", {"start": v(0.06, -38.24) * mm, "mid": v(0.56, -39.3) * mm, "end": v(1.18, -40.28) * mm});
            skPoint(sketch, "E16.24.15.0", {"position": v(3.98, -37.9) * mm});
            skPoint(sketch, "E16.27.15.0", {"position": v(1.44, -40.61) * mm});
            skPoint(sketch, "E16.28.15.0", {"position": v(3.76, -35.36) * mm});
            skLineSegment(sketch, "E16.29.15.0", {"start": v(0, -37.96) * mm, "end": v(0, -36.31) * mm});
            skArc(sketch, "E16.32.15.0", {"start": v(1.18, -40.28) * mm, "mid": v(1.47, -40.52) * mm, "end": v(1.84, -40.6) * mm});
            skArc(sketch, "E16.36.15.0", {"start": v(2.41, -40.56) * mm, "mid": v(2.77, -40.45) * mm, "end": v(3.03, -40.18) * mm});
            skLineSegment(sketch, "E16.40.15.0", {"start": v(2.41, -40.56) * mm, "end": v(2.13, -40.58) * mm});
            skLineSegment(sketch, "E16.43.15.0", {"start": v(1.84, -40.6) * mm, "end": v(2.13, -40.58) * mm});
            skArc(sketch, "E16.46.15.0", {"start": v(3.94, -38.04) * mm, "mid": v(3.97, -37.9) * mm, "end": v(3.97, -37.75) * mm});
            skArc(sketch, "E16.50.15.0", {"start": v(0, -37.96) * mm, "mid": v(0.01, -38.1) * mm, "end": v(0.06, -38.24) * mm});
            skArc(sketch, "E16.1.16.0", {"start": v(6.66, -34.93) * mm, "mid": v(9.22, -34.34) * mm, "end": v(11.73, -33.57) * mm});
            skLineSegment(sketch, "E16.5.16.0", {"start": v(11.73, -36.1) * mm, "end": v(11.22, -34.54) * mm});
            skArc(sketch, "E16.8.16.0", {"start": v(7.55, -35.52) * mm, "mid": v(7.23, -35.04) * mm, "end": v(6.66, -34.93) * mm});
            skPoint(sketch, "E16.12.16.0", {"position": v(7.92, -37.27) * mm});
            skPoint(sketch, "E16.13.16.0", {"position": v(7.4, -34.78) * mm});
            skArc(sketch, "E16.14.16.0", {"start": v(11.22, -34.54) * mm, "mid": v(11.26, -33.96) * mm, "end": v(11.7, -33.58) * mm});
            skArc(sketch, "E16.18.16.0", {"start": v(11.76, -36.39) * mm, "mid": v(11.61, -37.54) * mm, "end": v(11.32, -38.68) * mm});
            skPoint(sketch, "E16.22.16.0", {"position": v(11.18, -39.07) * mm});
            skArc(sketch, "E16.23.16.0", {"start": v(8, -37.4) * mm, "mid": v(8.72, -38.32) * mm, "end": v(9.53, -39.15) * mm});
            skPoint(sketch, "E16.24.16.0", {"position": v(11.77, -36.24) * mm});
            skPoint(sketch, "E16.27.16.0", {"position": v(9.85, -39.43) * mm});
            skPoint(sketch, "E16.28.16.0", {"position": v(11.03, -33.8) * mm});
            skLineSegment(sketch, "E16.29.16.0", {"start": v(7.9, -37.13) * mm, "end": v(7.55, -35.52) * mm});
            skArc(sketch, "E16.32.16.0", {"start": v(9.53, -39.15) * mm, "mid": v(9.87, -39.33) * mm, "end": v(10.24, -39.32) * mm});
            skArc(sketch, "E16.36.16.0", {"start": v(10.8, -39.18) * mm, "mid": v(11.12, -39) * mm, "end": v(11.32, -38.68) * mm});
            skLineSegment(sketch, "E16.40.16.0", {"start": v(10.8, -39.18) * mm, "end": v(10.52, -39.25) * mm});
            skLineSegment(sketch, "E16.43.16.0", {"start": v(10.24, -39.32) * mm, "end": v(10.52, -39.25) * mm});
            skArc(sketch, "E16.46.16.0", {"start": v(11.76, -36.39) * mm, "mid": v(11.76, -36.24) * mm, "end": v(11.73, -36.1) * mm});
            skArc(sketch, "E16.50.16.0", {"start": v(7.9, -37.13) * mm, "mid": v(7.94, -37.27) * mm, "end": v(8, -37.4) * mm});
            skArc(sketch, "E16.1.17.0", {"start": v(13.78, -32.78) * mm, "mid": v(16.16, -31.67) * mm, "end": v(18.46, -30.4) * mm});
            skLineSegment(sketch, "E16.5.17.0", {"start": v(18.98, -32.87) * mm, "end": v(18.16, -31.45) * mm});
            skArc(sketch, "E16.8.17.0", {"start": v(14.77, -33.17) * mm, "mid": v(14.35, -32.78) * mm, "end": v(13.78, -32.78) * mm});
            skPoint(sketch, "E16.12.17.0", {"position": v(15.5, -34.8) * mm});
            skPoint(sketch, "E16.13.17.0", {"position": v(14.46, -32.49) * mm});
            skArc(sketch, "E16.14.17.0", {"start": v(18.16, -31.45) * mm, "mid": v(18.08, -30.88) * mm, "end": v(18.42, -30.42) * mm});
            skArc(sketch, "E16.18.17.0", {"start": v(19.07, -33.14) * mm, "mid": v(19.16, -34.3) * mm, "end": v(19.11, -35.48) * mm});
            skPoint(sketch, "E16.22.17.0", {"position": v(19.06, -35.9) * mm});
            skArc(sketch, "E16.23.17.0", {"start": v(15.6, -34.91) * mm, "mid": v(16.5, -35.67) * mm, "end": v(17.47, -36.32) * mm});
            skPoint(sketch, "E16.24.17.0", {"position": v(19.05, -33) * mm});
            skPoint(sketch, "E16.27.17.0", {"position": v(17.83, -36.52) * mm});
            skPoint(sketch, "E16.28.17.0", {"position": v(17.82, -30.77) * mm});
            skLineSegment(sketch, "E16.29.17.0", {"start": v(15.44, -34.67) * mm, "end": v(14.77, -33.17) * mm});
            skArc(sketch, "E16.32.17.0", {"start": v(17.47, -36.32) * mm, "mid": v(17.83, -36.42) * mm, "end": v(18.2, -36.34) * mm});
            skArc(sketch, "E16.36.17.0", {"start": v(18.7, -36.08) * mm, "mid": v(18.98, -35.83) * mm, "end": v(19.11, -35.48) * mm});
            skLineSegment(sketch, "E16.40.17.0", {"start": v(18.7, -36.08) * mm, "end": v(18.45, -36.2) * mm});
            skLineSegment(sketch, "E16.43.17.0", {"start": v(18.2, -36.34) * mm, "end": v(18.45, -36.2) * mm});
            skArc(sketch, "E16.46.17.0", {"start": v(19.07, -33.14) * mm, "mid": v(19.04, -33) * mm, "end": v(18.98, -32.87) * mm});
            skArc(sketch, "E16.50.17.0", {"start": v(15.44, -34.67) * mm, "mid": v(15.5, -34.8) * mm, "end": v(15.6, -34.91) * mm});
            skArc(sketch, "E16.1.18.0", {"start": v(20.3, -29.2) * mm, "mid": v(22.4, -27.62) * mm, "end": v(24.37, -25.9) * mm});
            skLineSegment(sketch, "E16.5.18.0", {"start": v(25.4, -28.2) * mm, "end": v(24.3, -26.99) * mm});
            skArc(sketch, "E16.8.18.0", {"start": v(21.34, -29.38) * mm, "mid": v(20.86, -29.08) * mm, "end": v(20.3, -29.2) * mm});
            skPoint(sketch, "E16.12.18.0", {"position": v(22.4, -30.82) * mm});
            skPoint(sketch, "E16.13.18.0", {"position": v(20.9, -28.77) * mm});
            skArc(sketch, "E16.14.18.0", {"start": v(24.3, -26.99) * mm, "mid": v(24.1, -26.44) * mm, "end": v(24.34, -25.92) * mm});
            skArc(sketch, "E16.18.18.0", {"start": v(25.55, -28.45) * mm, "mid": v(25.88, -29.57) * mm, "end": v(26.07, -30.73) * mm});
            skPoint(sketch, "E16.22.18.0", {"position": v(26.1, -31.15) * mm});
            skArc(sketch, "E16.23.18.0", {"start": v(22.52, -30.9) * mm, "mid": v(23.55, -31.46) * mm, "end": v(24.63, -31.9) * mm});
            skPoint(sketch, "E16.24.18.0", {"position": v(25.5, -28.31) * mm});
            skPoint(sketch, "E16.27.18.0", {"position": v(25.04, -32.01) * mm});
            skPoint(sketch, "E16.28.18.0", {"position": v(23.83, -26.4) * mm});
            skLineSegment(sketch, "E16.29.18.0", {"start": v(22.3, -30.7) * mm, "end": v(21.34, -29.38) * mm});
            skArc(sketch, "E16.32.18.0", {"start": v(24.63, -31.9) * mm, "mid": v(25, -31.92) * mm, "end": v(25.35, -31.76) * mm});
            skArc(sketch, "E16.36.18.0", {"start": v(25.8, -31.4) * mm, "mid": v(26.02, -31.1) * mm, "end": v(26.07, -30.73) * mm});
            skLineSegment(sketch, "E16.40.18.0", {"start": v(25.8, -31.4) * mm, "end": v(25.57, -31.58) * mm});
            skLineSegment(sketch, "E16.43.18.0", {"start": v(25.35, -31.76) * mm, "end": v(25.57, -31.58) * mm});
            skArc(sketch, "E16.46.18.0", {"start": v(25.55, -28.45) * mm, "mid": v(25.48, -28.32) * mm, "end": v(25.4, -28.2) * mm});
            skArc(sketch, "E16.50.18.0", {"start": v(22.3, -30.7) * mm, "mid": v(22.4, -30.82) * mm, "end": v(22.52, -30.9) * mm});
            skArc(sketch, "E16.1.19.0", {"start": v(25.92, -24.34) * mm, "mid": v(27.65, -22.36) * mm, "end": v(29.22, -20.26) * mm});
            skLineSegment(sketch, "E16.5.19.0", {"start": v(30.7, -22.3) * mm, "end": v(29.38, -21.34) * mm});
            skArc(sketch, "E16.8.19.0", {"start": v(26.99, -24.3) * mm, "mid": v(26.44, -24.1) * mm, "end": v(25.92, -24.34) * mm});
            skPoint(sketch, "E16.12.19.0", {"position": v(28.31, -25.5) * mm});
            skPoint(sketch, "E16.13.19.0", {"position": v(26.43, -23.8) * mm});
            skArc(sketch, "E16.14.19.0", {"start": v(29.38, -21.34) * mm, "mid": v(29.08, -20.86) * mm, "end": v(29.2, -20.3) * mm});
            skArc(sketch, "E16.18.19.0", {"start": v(30.9, -22.52) * mm, "mid": v(31.46, -23.55) * mm, "end": v(31.9, -24.63) * mm});
            skPoint(sketch, "E16.22.19.0", {"position": v(32.01, -25.04) * mm});
            skArc(sketch, "E16.23.19.0", {"start": v(28.45, -25.55) * mm, "mid": v(29.57, -25.88) * mm, "end": v(30.73, -26.07) * mm});
            skPoint(sketch, "E16.24.19.0", {"position": v(30.82, -22.4) * mm});
            skPoint(sketch, "E16.27.19.0", {"position": v(31.15, -26.1) * mm});
            skPoint(sketch, "E16.28.19.0", {"position": v(28.8, -20.87) * mm});
            skLineSegment(sketch, "E16.29.19.0", {"start": v(28.2, -25.4) * mm, "end": v(26.99, -24.3) * mm});
            skArc(sketch, "E16.32.19.0", {"start": v(30.73, -26.07) * mm, "mid": v(31.1, -26.02) * mm, "end": v(31.4, -25.8) * mm});
            skArc(sketch, "E16.36.19.0", {"start": v(31.76, -25.35) * mm, "mid": v(31.92, -25) * mm, "end": v(31.9, -24.63) * mm});
            skLineSegment(sketch, "E16.40.19.0", {"start": v(31.76, -25.35) * mm, "end": v(31.58, -25.57) * mm});
            skLineSegment(sketch, "E16.43.19.0", {"start": v(31.4, -25.8) * mm, "end": v(31.58, -25.57) * mm});
            skArc(sketch, "E16.46.19.0", {"start": v(30.9, -22.52) * mm, "mid": v(30.82, -22.4) * mm, "end": v(30.7, -22.3) * mm});
            skArc(sketch, "E16.50.19.0", {"start": v(28.2, -25.4) * mm, "mid": v(28.32, -25.48) * mm, "end": v(28.45, -25.55) * mm});
            skArc(sketch, "E16.1.20.0", {"start": v(30.42, -18.42) * mm, "mid": v(31.7, -16.13) * mm, "end": v(32.8, -13.74) * mm});
            skLineSegment(sketch, "E16.5.20.0", {"start": v(34.67, -15.44) * mm, "end": v(33.17, -14.77) * mm});
            skArc(sketch, "E16.8.20.0", {"start": v(31.45, -18.16) * mm, "mid": v(30.88, -18.08) * mm, "end": v(30.42, -18.42) * mm});
            skPoint(sketch, "E16.12.20.0", {"position": v(33, -19.05) * mm});
            skPoint(sketch, "E16.13.20.0", {"position": v(30.8, -17.78) * mm});
            skArc(sketch, "E16.14.20.0", {"start": v(33.17, -14.77) * mm, "mid": v(32.78, -14.35) * mm, "end": v(32.78, -13.78) * mm});
            skArc(sketch, "E16.18.20.0", {"start": v(34.91, -15.6) * mm, "mid": v(35.67, -16.5) * mm, "end": v(36.32, -17.47) * mm});
            skPoint(sketch, "E16.22.20.0", {"position": v(36.52, -17.83) * mm});
            skArc(sketch, "E16.23.20.0", {"start": v(33.14, -19.07) * mm, "mid": v(34.3, -19.16) * mm, "end": v(35.48, -19.11) * mm});
            skPoint(sketch, "E16.24.20.0", {"position": v(34.8, -15.5) * mm});
            skPoint(sketch, "E16.27.20.0", {"position": v(35.9, -19.06) * mm});
            skPoint(sketch, "E16.28.20.0", {"position": v(32.5, -14.42) * mm});
            skLineSegment(sketch, "E16.29.20.0", {"start": v(32.87, -18.98) * mm, "end": v(31.45, -18.16) * mm});
            skArc(sketch, "E16.32.20.0", {"start": v(35.48, -19.11) * mm, "mid": v(35.83, -18.98) * mm, "end": v(36.08, -18.7) * mm});
            skArc(sketch, "E16.36.20.0", {"start": v(36.34, -18.2) * mm, "mid": v(36.42, -17.83) * mm, "end": v(36.32, -17.47) * mm});
            skLineSegment(sketch, "E16.40.20.0", {"start": v(36.34, -18.2) * mm, "end": v(36.2, -18.45) * mm});
            skLineSegment(sketch, "E16.43.20.0", {"start": v(36.08, -18.7) * mm, "end": v(36.2, -18.45) * mm});
            skArc(sketch, "E16.46.20.0", {"start": v(34.91, -15.6) * mm, "mid": v(34.8, -15.5) * mm, "end": v(34.67, -15.44) * mm});
            skArc(sketch, "E16.50.20.0", {"start": v(32.87, -18.98) * mm, "mid": v(33, -19.04) * mm, "end": v(33.14, -19.07) * mm});
            skArc(sketch, "E16.1.21.0", {"start": v(33.58, -11.7) * mm, "mid": v(34.35, -9.18) * mm, "end": v(34.94, -6.62) * mm});
            skLineSegment(sketch, "E16.5.21.0", {"start": v(37.13, -7.9) * mm, "end": v(35.52, -7.55) * mm});
            skArc(sketch, "E16.8.21.0", {"start": v(34.54, -11.22) * mm, "mid": v(33.96, -11.26) * mm, "end": v(33.58, -11.7) * mm});
            skPoint(sketch, "E16.12.21.0", {"position": v(36.24, -11.77) * mm});
            skPoint(sketch, "E16.13.21.0", {"position": v(33.82, -10.99) * mm});
            skArc(sketch, "E16.14.21.0", {"start": v(35.52, -7.55) * mm, "mid": v(35.04, -7.23) * mm, "end": v(34.93, -6.66) * mm});
            skArc(sketch, "E16.18.21.0", {"start": v(37.4, -8) * mm, "mid": v(38.32, -8.72) * mm, "end": v(39.15, -9.53) * mm});
            skPoint(sketch, "E16.22.21.0", {"position": v(39.43, -9.85) * mm});
            skArc(sketch, "E16.23.21.0", {"start": v(36.39, -11.76) * mm, "mid": v(37.54, -11.61) * mm, "end": v(38.68, -11.32) * mm});
            skPoint(sketch, "E16.24.21.0", {"position": v(37.27, -7.92) * mm});
            skPoint(sketch, "E16.27.21.0", {"position": v(39.07, -11.18) * mm});
            skPoint(sketch, "E16.28.21.0", {"position": v(34.8, -7.35) * mm});
            skLineSegment(sketch, "E16.29.21.0", {"start": v(36.1, -11.73) * mm, "end": v(34.54, -11.22) * mm});
            skArc(sketch, "E16.32.21.0", {"start": v(38.68, -11.32) * mm, "mid": v(39, -11.12) * mm, "end": v(39.18, -10.8) * mm});
            skArc(sketch, "E16.36.21.0", {"start": v(39.32, -10.24) * mm, "mid": v(39.33, -9.87) * mm, "end": v(39.15, -9.53) * mm});
            skLineSegment(sketch, "E16.40.21.0", {"start": v(39.32, -10.24) * mm, "end": v(39.25, -10.52) * mm});
            skLineSegment(sketch, "E16.43.21.0", {"start": v(39.18, -10.8) * mm, "end": v(39.25, -10.52) * mm});
            skArc(sketch, "E16.46.21.0", {"start": v(37.4, -8) * mm, "mid": v(37.27, -7.94) * mm, "end": v(37.13, -7.9) * mm});
            skArc(sketch, "E16.50.21.0", {"start": v(36.1, -11.73) * mm, "mid": v(36.24, -11.76) * mm, "end": v(36.39, -11.76) * mm});
            skArc(sketch, "E16.1.22.0", {"start": v(35.28, -4.46) * mm, "mid": v(35.51, -1.84) * mm, "end": v(35.55, 0.79) * mm});
            skLineSegment(sketch, "E16.5.22.0", {"start": v(37.96, 0) * mm, "end": v(36.31, 0) * mm});
            skArc(sketch, "E16.8.22.0", {"start": v(36.12, -3.8) * mm, "mid": v(35.56, -3.96) * mm, "end": v(35.28, -4.46) * mm});
            skPoint(sketch, "E16.12.22.0", {"position": v(37.9, -3.98) * mm});
            skPoint(sketch, "E16.13.22.0", {"position": v(35.37, -3.72) * mm});
            skArc(sketch, "E16.14.22.0", {"start": v(36.31, 0) * mm, "mid": v(35.78, 0.22) * mm, "end": v(35.55, 0.75) * mm});
            skArc(sketch, "E16.18.22.0", {"start": v(38.24, -0.06) * mm, "mid": v(39.3, -0.56) * mm, "end": v(40.28, -1.18) * mm});
            skPoint(sketch, "E16.22.22.0", {"position": v(40.61, -1.44) * mm});
            skArc(sketch, "E16.23.22.0", {"start": v(38.04, -3.94) * mm, "mid": v(39.14, -3.55) * mm, "end": v(40.18, -3.03) * mm});
            skPoint(sketch, "E16.24.22.0", {"position": v(38.1, 0) * mm});
            skPoint(sketch, "E16.27.22.0", {"position": v(40.54, -2.81) * mm});
            skPoint(sketch, "E16.28.22.0", {"position": v(35.56, 0.04) * mm});
            skLineSegment(sketch, "E16.29.22.0", {"start": v(37.75, -3.97) * mm, "end": v(36.12, -3.8) * mm});
            skArc(sketch, "E16.32.22.0", {"start": v(40.18, -3.03) * mm, "mid": v(40.45, -2.77) * mm, "end": v(40.56, -2.41) * mm});
            skArc(sketch, "E16.36.22.0", {"start": v(40.6, -1.84) * mm, "mid": v(40.52, -1.47) * mm, "end": v(40.28, -1.18) * mm});
            skLineSegment(sketch, "E16.40.22.0", {"start": v(40.6, -1.84) * mm, "end": v(40.58, -2.13) * mm});
            skLineSegment(sketch, "E16.43.22.0", {"start": v(40.56, -2.41) * mm, "end": v(40.58, -2.13) * mm});
            skArc(sketch, "E16.46.22.0", {"start": v(38.24, -0.06) * mm, "mid": v(38.1, -0.01) * mm, "end": v(37.96, 0) * mm});
            skArc(sketch, "E16.50.22.0", {"start": v(37.75, -3.97) * mm, "mid": v(37.9, -3.97) * mm, "end": v(38.04, -3.94) * mm});
            skArc(sketch, "E16.1.23.0", {"start": v(35.44, 2.97) * mm, "mid": v(35.12, 5.58) * mm, "end": v(34.61, 8.16) * mm});
            skLineSegment(sketch, "E16.5.23.0", {"start": v(37.13, 7.9) * mm, "end": v(35.52, 7.55) * mm});
            skArc(sketch, "E16.8.23.0", {"start": v(36.12, 3.8) * mm, "mid": v(35.6, 3.52) * mm, "end": v(35.44, 2.97) * mm});
            skPoint(sketch, "E16.12.23.0", {"position": v(37.9, 3.98) * mm});
            skPoint(sketch, "E16.13.23.0", {"position": v(35.37, 3.72) * mm});
            skArc(sketch, "E16.14.23.0", {"start": v(35.52, 7.55) * mm, "mid": v(34.95, 7.65) * mm, "end": v(34.62, 8.12) * mm});
            skArc(sketch, "E16.18.23.0", {"start": v(37.42, 7.9) * mm, "mid": v(38.55, 7.62) * mm, "end": v(39.65, 7.22) * mm});
            skPoint(sketch, "E16.22.23.0", {"position": v(40.03, 7.04) * mm});
            skArc(sketch, "E16.23.23.0", {"start": v(38.02, 4.05) * mm, "mid": v(39.02, 4.66) * mm, "end": v(39.94, 5.39) * mm});
            skPoint(sketch, "E16.24.23.0", {"position": v(37.27, 7.92) * mm});
            skPoint(sketch, "E16.27.23.0", {"position": v(40.24, 5.68) * mm});
            skPoint(sketch, "E16.28.23.0", {"position": v(34.77, 7.43) * mm});
            skLineSegment(sketch, "E16.29.23.0", {"start": v(37.75, 3.97) * mm, "end": v(36.12, 3.8) * mm});
            skArc(sketch, "E16.32.23.0", {"start": v(39.94, 5.39) * mm, "mid": v(40.14, 5.7) * mm, "end": v(40.18, 6.07) * mm});
            skArc(sketch, "E16.36.23.0", {"start": v(40.09, 6.64) * mm, "mid": v(39.94, 6.98) * mm, "end": v(39.65, 7.22) * mm});
            skLineSegment(sketch, "E16.40.23.0", {"start": v(40.09, 6.64) * mm, "end": v(40.13, 6.36) * mm});
            skLineSegment(sketch, "E16.43.23.0", {"start": v(40.18, 6.07) * mm, "end": v(40.13, 6.36) * mm});
            skArc(sketch, "E16.46.23.0", {"start": v(37.42, 7.9) * mm, "mid": v(37.27, 7.9) * mm, "end": v(37.13, 7.9) * mm});
            skArc(sketch, "E16.50.23.0", {"start": v(37.75, 3.97) * mm, "mid": v(37.9, 4) * mm, "end": v(38.02, 4.05) * mm});
            skArc(sketch, "E16.1.24.0", {"start": v(34.04, 10.28) * mm, "mid": v(33.2, 12.76) * mm, "end": v(32.16, 15.18) * mm});
            skLineSegment(sketch, "E16.5.24.0", {"start": v(34.67, 15.44) * mm, "end": v(33.17, 14.77) * mm});
            skArc(sketch, "E16.8.24.0", {"start": v(34.54, 11.22) * mm, "mid": v(34.1, 10.85) * mm, "end": v(34.04, 10.28) * mm});
            skPoint(sketch, "E16.12.24.0", {"position": v(36.24, 11.77) * mm});
            skPoint(sketch, "E16.13.24.0", {"position": v(33.82, 10.99) * mm});
            skArc(sketch, "E16.14.24.0", {"start": v(33.17, 14.77) * mm, "mid": v(32.6, 14.75) * mm, "end": v(32.18, 15.14) * mm});
            skArc(sketch, "E16.18.24.0", {"start": v(34.96, 15.5) * mm, "mid": v(36.12, 15.47) * mm, "end": v(37.28, 15.3) * mm});
            skPoint(sketch, "E16.22.24.0", {"position": v(37.69, 15.2) * mm});
            skArc(sketch, "E16.23.24.0", {"start": v(36.35, 11.87) * mm, "mid": v(37.2, 12.67) * mm, "end": v(37.94, 13.57) * mm});
            skPoint(sketch, "E16.24.24.0", {"position": v(34.8, 15.5) * mm});
            skPoint(sketch, "E16.27.24.0", {"position": v(38.18, 13.92) * mm});
            skPoint(sketch, "E16.28.24.0", {"position": v(32.47, 14.5) * mm});
            skLineSegment(sketch, "E16.29.24.0", {"start": v(36.1, 11.73) * mm, "end": v(34.54, 11.22) * mm});
            skArc(sketch, "E16.32.24.0", {"start": v(37.94, 13.57) * mm, "mid": v(38.08, 13.92) * mm, "end": v(38.04, 14.3) * mm});
            skArc(sketch, "E16.36.24.0", {"start": v(37.83, 14.83) * mm, "mid": v(37.62, 15.14) * mm, "end": v(37.28, 15.3) * mm});
            skLineSegment(sketch, "E16.40.24.0", {"start": v(37.83, 14.83) * mm, "end": v(37.94, 14.56) * mm});
            skLineSegment(sketch, "E16.43.24.0", {"start": v(38.04, 14.3) * mm, "end": v(37.94, 14.56) * mm});
            skArc(sketch, "E16.46.24.0", {"start": v(34.96, 15.5) * mm, "mid": v(34.81, 15.48) * mm, "end": v(34.67, 15.44) * mm});
            skArc(sketch, "E16.50.24.0", {"start": v(36.1, 11.73) * mm, "mid": v(36.23, 11.79) * mm, "end": v(36.35, 11.87) * mm});
            skArc(sketch, "E16.1.25.0", {"start": v(31.16, 17.13) * mm, "mid": v(29.81, 19.38) * mm, "end": v(28.3, 21.53) * mm});
            skLineSegment(sketch, "E16.5.25.0", {"start": v(30.7, 22.3) * mm, "end": v(29.38, 21.34) * mm});
            skArc(sketch, "E16.8.25.0", {"start": v(31.45, 18.16) * mm, "mid": v(31.1, 17.7) * mm, "end": v(31.16, 17.13) * mm});
            skPoint(sketch, "E16.12.25.0", {"position": v(33, 19.05) * mm});
            skPoint(sketch, "E16.13.25.0", {"position": v(30.8, 17.78) * mm});
            skArc(sketch, "E16.14.25.0", {"start": v(29.38, 21.34) * mm, "mid": v(28.82, 21.2) * mm, "end": v(28.32, 21.5) * mm});
            skArc(sketch, "E16.18.25.0", {"start": v(30.97, 22.43) * mm, "mid": v(32.12, 22.65) * mm, "end": v(33.28, 22.72) * mm});
            skPoint(sketch, "E16.22.25.0", {"position": v(33.7, 22.7) * mm});
            skArc(sketch, "E16.23.25.0", {"start": v(33.09, 19.17) * mm, "mid": v(33.75, 20.13) * mm, "end": v(34.3, 21.17) * mm});
            skPoint(sketch, "E16.24.25.0", {"position": v(30.82, 22.4) * mm});
            skPoint(sketch, "E16.27.25.0", {"position": v(34.45, 21.55) * mm});
            skPoint(sketch, "E16.28.25.0", {"position": v(28.74, 20.94) * mm});
            skLineSegment(sketch, "E16.29.25.0", {"start": v(32.87, 18.98) * mm, "end": v(31.45, 18.16) * mm});
            skArc(sketch, "E16.32.25.0", {"start": v(34.3, 21.17) * mm, "mid": v(34.35, 21.54) * mm, "end": v(34.23, 21.9) * mm});
            skArc(sketch, "E16.36.25.0", {"start": v(33.92, 22.37) * mm, "mid": v(33.65, 22.63) * mm, "end": v(33.28, 22.72) * mm});
            skLineSegment(sketch, "E16.40.25.0", {"start": v(33.92, 22.37) * mm, "end": v(34.08, 22.13) * mm});
            skLineSegment(sketch, "E16.43.25.0", {"start": v(34.23, 21.9) * mm, "end": v(34.08, 22.13) * mm});
            skArc(sketch, "E16.46.25.0", {"start": v(30.97, 22.43) * mm, "mid": v(30.83, 22.38) * mm, "end": v(30.7, 22.3) * mm});
            skArc(sketch, "E16.50.25.0", {"start": v(32.87, 18.98) * mm, "mid": v(32.99, 19.06) * mm, "end": v(33.09, 19.17) * mm});
            skArc(sketch, "E16.1.26.0", {"start": v(26.92, 23.23) * mm, "mid": v(25.13, 25.16) * mm, "end": v(23.2, 26.95) * mm});
            skLineSegment(sketch, "E16.5.26.0", {"start": v(25.4, 28.2) * mm, "end": v(24.3, 26.99) * mm});
            skArc(sketch, "E16.8.26.0", {"start": v(26.99, 24.3) * mm, "mid": v(26.74, 23.78) * mm, "end": v(26.92, 23.23) * mm});
            skPoint(sketch, "E16.12.26.0", {"position": v(28.31, 25.5) * mm});
            skPoint(sketch, "E16.13.26.0", {"position": v(26.43, 23.8) * mm});
            skArc(sketch, "E16.14.26.0", {"start": v(24.3, 26.99) * mm, "mid": v(23.78, 26.74) * mm, "end": v(23.23, 26.92) * mm});
            skArc(sketch, "E16.18.26.0", {"start": v(25.63, 28.38) * mm, "mid": v(26.7, 28.83) * mm, "end": v(27.83, 29.14) * mm});
            skPoint(sketch, "E16.22.26.0", {"position": v(28.25, 29.22) * mm});
            skArc(sketch, "E16.23.26.0", {"start": v(28.38, 25.63) * mm, "mid": v(28.83, 26.7) * mm, "end": v(29.14, 27.83) * mm});
            skPoint(sketch, "E16.24.26.0", {"position": v(25.5, 28.31) * mm});
            skPoint(sketch, "E16.27.26.0", {"position": v(29.22, 28.25) * mm});
            skPoint(sketch, "E16.28.26.0", {"position": v(23.76, 26.45) * mm});
            skLineSegment(sketch, "E16.29.26.0", {"start": v(28.2, 25.4) * mm, "end": v(26.99, 24.3) * mm});
            skArc(sketch, "E16.32.26.0", {"start": v(29.14, 27.83) * mm, "mid": v(29.13, 28.2) * mm, "end": v(28.93, 28.53) * mm});
            skArc(sketch, "E16.36.26.0", {"start": v(28.53, 28.93) * mm, "mid": v(28.2, 29.13) * mm, "end": v(27.83, 29.14) * mm});
            skLineSegment(sketch, "E16.40.26.0", {"start": v(28.53, 28.93) * mm, "end": v(28.73, 28.73) * mm});
            skLineSegment(sketch, "E16.43.26.0", {"start": v(28.93, 28.53) * mm, "end": v(28.73, 28.73) * mm});
            skArc(sketch, "E16.46.26.0", {"start": v(25.63, 28.38) * mm, "mid": v(25.5, 28.3) * mm, "end": v(25.4, 28.2) * mm});
            skArc(sketch, "E16.50.26.0", {"start": v(28.2, 25.4) * mm, "mid": v(28.3, 25.5) * mm, "end": v(28.38, 25.63) * mm});
            skArc(sketch, "E16.1.27.0", {"start": v(21.5, 28.32) * mm, "mid": v(19.35, 29.83) * mm, "end": v(17.1, 31.18) * mm});
            skLineSegment(sketch, "E16.5.27.0", {"start": v(18.98, 32.87) * mm, "end": v(18.16, 31.45) * mm});
            skArc(sketch, "E16.8.27.0", {"start": v(21.34, 29.38) * mm, "mid": v(21.2, 28.82) * mm, "end": v(21.5, 28.32) * mm});
            skPoint(sketch, "E16.12.27.0", {"position": v(22.4, 30.82) * mm});
            skPoint(sketch, "E16.13.27.0", {"position": v(20.9, 28.77) * mm});
            skArc(sketch, "E16.14.27.0", {"start": v(18.16, 31.45) * mm, "mid": v(17.7, 31.1) * mm, "end": v(17.13, 31.16) * mm});
            skArc(sketch, "E16.18.27.0", {"start": v(19.17, 33.09) * mm, "mid": v(20.13, 33.75) * mm, "end": v(21.17, 34.3) * mm});
            skPoint(sketch, "E16.22.27.0", {"position": v(21.55, 34.45) * mm});
            skArc(sketch, "E16.23.27.0", {"start": v(22.43, 30.97) * mm, "mid": v(22.65, 32.12) * mm, "end": v(22.72, 33.28) * mm});
            skPoint(sketch, "E16.24.27.0", {"position": v(19.05, 33) * mm});
            skPoint(sketch, "E16.27.27.0", {"position": v(22.7, 33.7) * mm});
            skPoint(sketch, "E16.28.27.0", {"position": v(17.74, 30.82) * mm});
            skLineSegment(sketch, "E16.29.27.0", {"start": v(22.3, 30.7) * mm, "end": v(21.34, 29.38) * mm});
            skArc(sketch, "E16.32.27.0", {"start": v(22.72, 33.28) * mm, "mid": v(22.63, 33.65) * mm, "end": v(22.37, 33.92) * mm});
            skArc(sketch, "E16.36.27.0", {"start": v(21.9, 34.23) * mm, "mid": v(21.54, 34.35) * mm, "end": v(21.17, 34.3) * mm});
            skLineSegment(sketch, "E16.40.27.0", {"start": v(21.9, 34.23) * mm, "end": v(22.13, 34.08) * mm});
            skLineSegment(sketch, "E16.43.27.0", {"start": v(22.37, 33.92) * mm, "end": v(22.13, 34.08) * mm});
            skArc(sketch, "E16.46.27.0", {"start": v(19.17, 33.09) * mm, "mid": v(19.06, 32.99) * mm, "end": v(18.98, 32.87) * mm});
            skArc(sketch, "E16.50.27.0", {"start": v(22.3, 30.7) * mm, "mid": v(22.38, 30.83) * mm, "end": v(22.43, 30.97) * mm});
            skArc(sketch, "E16.1.28.0", {"start": v(15.14, 32.18) * mm, "mid": v(12.72, 33.2) * mm, "end": v(10.24, 34.05) * mm});
            skLineSegment(sketch, "E16.5.28.0", {"start": v(11.73, 36.1) * mm, "end": v(11.22, 34.54) * mm});
            skArc(sketch, "E16.8.28.0", {"start": v(14.77, 33.17) * mm, "mid": v(14.75, 32.6) * mm, "end": v(15.14, 32.18) * mm});
            skPoint(sketch, "E16.12.28.0", {"position": v(15.5, 34.8) * mm});
            skPoint(sketch, "E16.13.28.0", {"position": v(14.46, 32.49) * mm});
            skArc(sketch, "E16.14.28.0", {"start": v(11.22, 34.54) * mm, "mid": v(10.85, 34.1) * mm, "end": v(10.28, 34.04) * mm});
            skArc(sketch, "E16.18.28.0", {"start": v(11.87, 36.35) * mm, "mid": v(12.67, 37.2) * mm, "end": v(13.57, 37.94) * mm});
            skPoint(sketch, "E16.22.28.0", {"position": v(13.92, 38.18) * mm});
            skArc(sketch, "E16.23.28.0", {"start": v(15.5, 34.96) * mm, "mid": v(15.47, 36.12) * mm, "end": v(15.3, 37.28) * mm});
            skPoint(sketch, "E16.24.28.0", {"position": v(11.77, 36.24) * mm});
            skPoint(sketch, "E16.27.28.0", {"position": v(15.2, 37.69) * mm});
            skPoint(sketch, "E16.28.28.0", {"position": v(10.95, 33.83) * mm});
            skLineSegment(sketch, "E16.29.28.0", {"start": v(15.44, 34.67) * mm, "end": v(14.77, 33.17) * mm});
            skArc(sketch, "E16.32.28.0", {"start": v(15.3, 37.28) * mm, "mid": v(15.14, 37.62) * mm, "end": v(14.83, 37.83) * mm});
            skArc(sketch, "E16.36.28.0", {"start": v(14.3, 38.04) * mm, "mid": v(13.92, 38.08) * mm, "end": v(13.57, 37.94) * mm});
            skLineSegment(sketch, "E16.40.28.0", {"start": v(14.3, 38.04) * mm, "end": v(14.56, 37.94) * mm});
            skLineSegment(sketch, "E16.43.28.0", {"start": v(14.83, 37.83) * mm, "end": v(14.56, 37.94) * mm});
            skArc(sketch, "E16.46.28.0", {"start": v(11.87, 36.35) * mm, "mid": v(11.79, 36.23) * mm, "end": v(11.73, 36.1) * mm});
            skArc(sketch, "E16.50.28.0", {"start": v(15.44, 34.67) * mm, "mid": v(15.48, 34.81) * mm, "end": v(15.5, 34.96) * mm});
            skArc(sketch, "E16.1.29.0", {"start": v(8.12, 34.62) * mm, "mid": v(5.54, 35.13) * mm, "end": v(2.93, 35.44) * mm});
            skLineSegment(sketch, "E16.5.29.0", {"start": v(3.97, 37.75) * mm, "end": v(3.8, 36.12) * mm});
            skArc(sketch, "E16.8.29.0", {"start": v(7.55, 35.52) * mm, "mid": v(7.65, 34.95) * mm, "end": v(8.12, 34.62) * mm});
            skPoint(sketch, "E16.12.29.0", {"position": v(7.92, 37.27) * mm});
            skPoint(sketch, "E16.13.29.0", {"position": v(7.4, 34.78) * mm});
            skArc(sketch, "E16.14.29.0", {"start": v(3.8, 36.12) * mm, "mid": v(3.52, 35.6) * mm, "end": v(2.97, 35.44) * mm});
            skArc(sketch, "E16.18.29.0", {"start": v(4.05, 38.02) * mm, "mid": v(4.66, 39.02) * mm, "end": v(5.39, 39.94) * mm});
            skPoint(sketch, "E16.22.29.0", {"position": v(5.68, 40.24) * mm});
            skArc(sketch, "E16.23.29.0", {"start": v(7.9, 37.42) * mm, "mid": v(7.62, 38.55) * mm, "end": v(7.22, 39.65) * mm});
            skPoint(sketch, "E16.24.29.0", {"position": v(3.98, 37.9) * mm});
            skPoint(sketch, "E16.27.29.0", {"position": v(7.04, 40.03) * mm});
            skPoint(sketch, "E16.28.29.0", {"position": v(3.67, 35.37) * mm});
            skLineSegment(sketch, "E16.29.29.0", {"start": v(7.9, 37.13) * mm, "end": v(7.55, 35.52) * mm});
            skArc(sketch, "E16.32.29.0", {"start": v(7.22, 39.65) * mm, "mid": v(6.98, 39.94) * mm, "end": v(6.64, 40.09) * mm});
            skArc(sketch, "E16.36.29.0", {"start": v(6.07, 40.18) * mm, "mid": v(5.7, 40.14) * mm, "end": v(5.39, 39.94) * mm});
            skLineSegment(sketch, "E16.40.29.0", {"start": v(6.07, 40.18) * mm, "end": v(6.36, 40.13) * mm});
            skLineSegment(sketch, "E16.43.29.0", {"start": v(6.64, 40.09) * mm, "end": v(6.36, 40.13) * mm});
            skArc(sketch, "E16.46.29.0", {"start": v(4.05, 38.02) * mm, "mid": v(4, 37.9) * mm, "end": v(3.97, 37.75) * mm});
            skArc(sketch, "E16.50.29.0", {"start": v(7.9, 37.13) * mm, "mid": v(7.9, 37.27) * mm, "end": v(7.9, 37.42) * mm});
            skSolve(sketch);
        }
        {
            var Q0;
            Q0 = qSketchRegion(id + "F3", true);
            extrude(context, id + "F4", {"entities" : qUnion([Q0]), "operationType" : NewBodyOperationType.ADD, "oppositeDirection" : true, "depth" : 57.15 * mm});
        }
        {
            var Q0;
            Q0=makeQuery(id+"F4.opExtrude","CAP_FACE",FACE,{"disambiguationData":[OSD([sQuery(id+"F3.wireOp",EDGE,"E1.trimOffspring"),sQuery(id+"F3.wireOp",EDGE,"E2"),sQuery(id+"F3.wireOp",EDGE,"E3"),sQuery(id+"F3.wireOp",EDGE,"E4.MirrorCS"),sQuery(id+"F3.wireOp",EDGE,"E5.MirrorCS"),sQuery(id+"F3.wireOp",EDGE,"E7.filletArc"),sQuery(id+"F3.wireOp",EDGE,"E8"),sQuery(id+"F3.wireOp",EDGE,"E9.MirrorCS"),sQuery(id+"F3.wireOp",EDGE,"E10.MirrorCS"),sQuery(id+"F3.wireOp",EDGE,"E11.filletArc"),sQuery(id+"F3.wireOp",EDGE,"E12.filletArc"),sQuery(id+"F3.wireOp",EDGE,"E13.filletArc"),sQuery(id+"F3.wireOp",EDGE,"E14.filletArc")])],"isStart":false});
            var Q1;
            Q1=makeQuery(id+"F4.opExtrude","CAP_FACE",FACE,{"disambiguationData":[OSD([sQuery(id+"F3.wireOp",EDGE,"E15.1.1"),sQuery(id+"F3.wireOp",EDGE,"E15.1.2"),sQuery(id+"F3.wireOp",EDGE,"E15.1.3"),sQuery(id+"F3.wireOp",EDGE,"E15.1.6"),sQuery(id+"F3.wireOp",EDGE,"E15.1.7"),sQuery(id+"F3.wireOp",EDGE,"E15.1.9"),sQuery(id+"F3.wireOp",EDGE,"E15.1.12"),sQuery(id+"F3.wireOp",EDGE,"E15.1.13"),sQuery(id+"F3.wireOp",EDGE,"E15.1.14"),sQuery(id+"F3.wireOp",EDGE,"E15.1.15"),sQuery(id+"F3.wireOp",EDGE,"E15.1.16"),sQuery(id+"F3.wireOp",EDGE,"E15.1.17"),sQuery(id+"F3.wireOp",EDGE,"E15.1.18")])],"isStart":false});
            var Q2;
            Q2=makeQuery(id+"F4.opExtrude","CAP_FACE",FACE,{"disambiguationData":[OSD([sQuery(id+"F3.wireOp",EDGE,"E16.1.29.0"),sQuery(id+"F3.wireOp",EDGE,"E16.5.29.0"),sQuery(id+"F3.wireOp",EDGE,"E16.8.29.0"),sQuery(id+"F3.wireOp",EDGE,"E16.14.29.0"),sQuery(id+"F3.wireOp",EDGE,"E16.18.29.0"),sQuery(id+"F3.wireOp",EDGE,"E16.23.29.0"),sQuery(id+"F3.wireOp",EDGE,"E16.29.29.0"),sQuery(id+"F3.wireOp",EDGE,"E16.32.29.0"),sQuery(id+"F3.wireOp",EDGE,"E16.36.29.0"),sQuery(id+"F3.wireOp",EDGE,"E16.40.29.0"),sQuery(id+"F3.wireOp",EDGE,"E16.43.29.0"),sQuery(id+"F3.wireOp",EDGE,"E16.46.29.0"),sQuery(id+"F3.wireOp",EDGE,"E16.50.29.0")])],"isStart":false});
            var Q3;
            Q3=makeQuery(id+"F4.opExtrude","CAP_FACE",FACE,{"disambiguationData":[OSD([sQuery(id+"F3.wireOp",EDGE,"E16.1.28.0"),sQuery(id+"F3.wireOp",EDGE,"E16.5.28.0"),sQuery(id+"F3.wireOp",EDGE,"E16.8.28.0"),sQuery(id+"F3.wireOp",EDGE,"E16.14.28.0"),sQuery(id+"F3.wireOp",EDGE,"E16.18.28.0"),sQuery(id+"F3.wireOp",EDGE,"E16.23.28.0"),sQuery(id+"F3.wireOp",EDGE,"E16.29.28.0"),sQuery(id+"F3.wireOp",EDGE,"E16.32.28.0"),sQuery(id+"F3.wireOp",EDGE,"E16.36.28.0"),sQuery(id+"F3.wireOp",EDGE,"E16.40.28.0"),sQuery(id+"F3.wireOp",EDGE,"E16.43.28.0"),sQuery(id+"F3.wireOp",EDGE,"E16.46.28.0"),sQuery(id+"F3.wireOp",EDGE,"E16.50.28.0")])],"isStart":false});
            var Q4;
            Q4=makeQuery(id+"F4.opExtrude","CAP_FACE",FACE,{"disambiguationData":[OSD([sQuery(id+"F3.wireOp",EDGE,"E16.1.27.0"),sQuery(id+"F3.wireOp",EDGE,"E16.5.27.0"),sQuery(id+"F3.wireOp",EDGE,"E16.8.27.0"),sQuery(id+"F3.wireOp",EDGE,"E16.14.27.0"),sQuery(id+"F3.wireOp",EDGE,"E16.18.27.0"),sQuery(id+"F3.wireOp",EDGE,"E16.23.27.0"),sQuery(id+"F3.wireOp",EDGE,"E16.29.27.0"),sQuery(id+"F3.wireOp",EDGE,"E16.32.27.0"),sQuery(id+"F3.wireOp",EDGE,"E16.36.27.0"),sQuery(id+"F3.wireOp",EDGE,"E16.40.27.0"),sQuery(id+"F3.wireOp",EDGE,"E16.43.27.0"),sQuery(id+"F3.wireOp",EDGE,"E16.46.27.0"),sQuery(id+"F3.wireOp",EDGE,"E16.50.27.0")])],"isStart":false});
            var Q5;
            Q5=makeQuery(id+"F4.opExtrude","CAP_FACE",FACE,{"disambiguationData":[OSD([sQuery(id+"F3.wireOp",EDGE,"E16.1.26.0"),sQuery(id+"F3.wireOp",EDGE,"E16.5.26.0"),sQuery(id+"F3.wireOp",EDGE,"E16.8.26.0"),sQuery(id+"F3.wireOp",EDGE,"E16.14.26.0"),sQuery(id+"F3.wireOp",EDGE,"E16.18.26.0"),sQuery(id+"F3.wireOp",EDGE,"E16.23.26.0"),sQuery(id+"F3.wireOp",EDGE,"E16.29.26.0"),sQuery(id+"F3.wireOp",EDGE,"E16.32.26.0"),sQuery(id+"F3.wireOp",EDGE,"E16.36.26.0"),sQuery(id+"F3.wireOp",EDGE,"E16.40.26.0"),sQuery(id+"F3.wireOp",EDGE,"E16.43.26.0"),sQuery(id+"F3.wireOp",EDGE,"E16.46.26.0"),sQuery(id+"F3.wireOp",EDGE,"E16.50.26.0")])],"isStart":false});
            var Q6;
            Q6=makeQuery(id+"F4.opExtrude","CAP_FACE",FACE,{"disambiguationData":[OSD([sQuery(id+"F3.wireOp",EDGE,"E16.1.25.0"),sQuery(id+"F3.wireOp",EDGE,"E16.5.25.0"),sQuery(id+"F3.wireOp",EDGE,"E16.8.25.0"),sQuery(id+"F3.wireOp",EDGE,"E16.14.25.0"),sQuery(id+"F3.wireOp",EDGE,"E16.18.25.0"),sQuery(id+"F3.wireOp",EDGE,"E16.23.25.0"),sQuery(id+"F3.wireOp",EDGE,"E16.29.25.0"),sQuery(id+"F3.wireOp",EDGE,"E16.32.25.0"),sQuery(id+"F3.wireOp",EDGE,"E16.36.25.0"),sQuery(id+"F3.wireOp",EDGE,"E16.40.25.0"),sQuery(id+"F3.wireOp",EDGE,"E16.43.25.0"),sQuery(id+"F3.wireOp",EDGE,"E16.46.25.0"),sQuery(id+"F3.wireOp",EDGE,"E16.50.25.0")])],"isStart":false});
            var Q7;
            Q7=makeQuery(id+"F4.opExtrude","CAP_FACE",FACE,{"disambiguationData":[OSD([sQuery(id+"F3.wireOp",EDGE,"E15.2.1"),sQuery(id+"F3.wireOp",EDGE,"E15.2.2"),sQuery(id+"F3.wireOp",EDGE,"E15.2.3"),sQuery(id+"F3.wireOp",EDGE,"E15.2.6"),sQuery(id+"F3.wireOp",EDGE,"E15.2.7"),sQuery(id+"F3.wireOp",EDGE,"E15.2.9"),sQuery(id+"F3.wireOp",EDGE,"E15.2.12"),sQuery(id+"F3.wireOp",EDGE,"E15.2.13"),sQuery(id+"F3.wireOp",EDGE,"E15.2.14"),sQuery(id+"F3.wireOp",EDGE,"E15.2.15"),sQuery(id+"F3.wireOp",EDGE,"E15.2.16"),sQuery(id+"F3.wireOp",EDGE,"E15.2.17"),sQuery(id+"F3.wireOp",EDGE,"E15.2.18")])],"isStart":false});
            var Q8;
            Q8=makeQuery(id+"F4.opExtrude","CAP_FACE",FACE,{"disambiguationData":[OSD([sQuery(id+"F3.wireOp",EDGE,"E16.1.3.0"),sQuery(id+"F3.wireOp",EDGE,"E16.5.3.0"),sQuery(id+"F3.wireOp",EDGE,"E16.8.3.0"),sQuery(id+"F3.wireOp",EDGE,"E16.14.3.0"),sQuery(id+"F3.wireOp",EDGE,"E16.18.3.0"),sQuery(id+"F3.wireOp",EDGE,"E16.23.3.0"),sQuery(id+"F3.wireOp",EDGE,"E16.29.3.0"),sQuery(id+"F3.wireOp",EDGE,"E16.32.3.0"),sQuery(id+"F3.wireOp",EDGE,"E16.36.3.0"),sQuery(id+"F3.wireOp",EDGE,"E16.40.3.0"),sQuery(id+"F3.wireOp",EDGE,"E16.43.3.0"),sQuery(id+"F3.wireOp",EDGE,"E16.46.3.0"),sQuery(id+"F3.wireOp",EDGE,"E16.50.3.0")])],"isStart":false});
            var Q9;
            Q9=makeQuery(id+"F4.opExtrude","CAP_FACE",FACE,{"disambiguationData":[OSD([sQuery(id+"F3.wireOp",EDGE,"E16.1.4.0"),sQuery(id+"F3.wireOp",EDGE,"E16.5.4.0"),sQuery(id+"F3.wireOp",EDGE,"E16.8.4.0"),sQuery(id+"F3.wireOp",EDGE,"E16.14.4.0"),sQuery(id+"F3.wireOp",EDGE,"E16.18.4.0"),sQuery(id+"F3.wireOp",EDGE,"E16.23.4.0"),sQuery(id+"F3.wireOp",EDGE,"E16.29.4.0"),sQuery(id+"F3.wireOp",EDGE,"E16.32.4.0"),sQuery(id+"F3.wireOp",EDGE,"E16.36.4.0"),sQuery(id+"F3.wireOp",EDGE,"E16.40.4.0"),sQuery(id+"F3.wireOp",EDGE,"E16.43.4.0"),sQuery(id+"F3.wireOp",EDGE,"E16.46.4.0"),sQuery(id+"F3.wireOp",EDGE,"E16.50.4.0")])],"isStart":false});
            var Q10;
            Q10=makeQuery(id+"F4.opExtrude","CAP_FACE",FACE,{"disambiguationData":[OSD([sQuery(id+"F3.wireOp",EDGE,"E16.1.5.0"),sQuery(id+"F3.wireOp",EDGE,"E16.5.5.0"),sQuery(id+"F3.wireOp",EDGE,"E16.8.5.0"),sQuery(id+"F3.wireOp",EDGE,"E16.14.5.0"),sQuery(id+"F3.wireOp",EDGE,"E16.18.5.0"),sQuery(id+"F3.wireOp",EDGE,"E16.23.5.0"),sQuery(id+"F3.wireOp",EDGE,"E16.29.5.0"),sQuery(id+"F3.wireOp",EDGE,"E16.32.5.0"),sQuery(id+"F3.wireOp",EDGE,"E16.36.5.0"),sQuery(id+"F3.wireOp",EDGE,"E16.40.5.0"),sQuery(id+"F3.wireOp",EDGE,"E16.43.5.0"),sQuery(id+"F3.wireOp",EDGE,"E16.46.5.0"),sQuery(id+"F3.wireOp",EDGE,"E16.50.5.0")])],"isStart":false});
            var Q11;
            Q11=makeQuery(id+"F4.opExtrude","CAP_FACE",FACE,{"disambiguationData":[OSD([sQuery(id+"F3.wireOp",EDGE,"E16.1.7.0"),sQuery(id+"F3.wireOp",EDGE,"E16.5.7.0"),sQuery(id+"F3.wireOp",EDGE,"E16.8.7.0"),sQuery(id+"F3.wireOp",EDGE,"E16.14.7.0"),sQuery(id+"F3.wireOp",EDGE,"E16.18.7.0"),sQuery(id+"F3.wireOp",EDGE,"E16.23.7.0"),sQuery(id+"F3.wireOp",EDGE,"E16.29.7.0"),sQuery(id+"F3.wireOp",EDGE,"E16.32.7.0"),sQuery(id+"F3.wireOp",EDGE,"E16.36.7.0"),sQuery(id+"F3.wireOp",EDGE,"E16.40.7.0"),sQuery(id+"F3.wireOp",EDGE,"E16.43.7.0"),sQuery(id+"F3.wireOp",EDGE,"E16.46.7.0"),sQuery(id+"F3.wireOp",EDGE,"E16.50.7.0")])],"isStart":false});
            var Q12;
            Q12=makeQuery(id+"F4.opExtrude","CAP_FACE",FACE,{"disambiguationData":[OSD([sQuery(id+"F3.wireOp",EDGE,"E16.1.6.0"),sQuery(id+"F3.wireOp",EDGE,"E16.5.6.0"),sQuery(id+"F3.wireOp",EDGE,"E16.8.6.0"),sQuery(id+"F3.wireOp",EDGE,"E16.14.6.0"),sQuery(id+"F3.wireOp",EDGE,"E16.18.6.0"),sQuery(id+"F3.wireOp",EDGE,"E16.23.6.0"),sQuery(id+"F3.wireOp",EDGE,"E16.29.6.0"),sQuery(id+"F3.wireOp",EDGE,"E16.32.6.0"),sQuery(id+"F3.wireOp",EDGE,"E16.36.6.0"),sQuery(id+"F3.wireOp",EDGE,"E16.40.6.0"),sQuery(id+"F3.wireOp",EDGE,"E16.43.6.0"),sQuery(id+"F3.wireOp",EDGE,"E16.46.6.0"),sQuery(id+"F3.wireOp",EDGE,"E16.50.6.0")])],"isStart":false});
            var Q13;
            Q13=makeQuery(id+"F4.opExtrude","CAP_FACE",FACE,{"disambiguationData":[OSD([sQuery(id+"F3.wireOp",EDGE,"E16.1.9.0"),sQuery(id+"F3.wireOp",EDGE,"E16.5.9.0"),sQuery(id+"F3.wireOp",EDGE,"E16.8.9.0"),sQuery(id+"F3.wireOp",EDGE,"E16.14.9.0"),sQuery(id+"F3.wireOp",EDGE,"E16.18.9.0"),sQuery(id+"F3.wireOp",EDGE,"E16.23.9.0"),sQuery(id+"F3.wireOp",EDGE,"E16.29.9.0"),sQuery(id+"F3.wireOp",EDGE,"E16.32.9.0"),sQuery(id+"F3.wireOp",EDGE,"E16.36.9.0"),sQuery(id+"F3.wireOp",EDGE,"E16.40.9.0"),sQuery(id+"F3.wireOp",EDGE,"E16.43.9.0"),sQuery(id+"F3.wireOp",EDGE,"E16.46.9.0"),sQuery(id+"F3.wireOp",EDGE,"E16.50.9.0")])],"isStart":false});
            var Q14;
            Q14=makeQuery(id+"F4.opExtrude","CAP_FACE",FACE,{"disambiguationData":[OSD([sQuery(id+"F3.wireOp",EDGE,"E16.1.8.0"),sQuery(id+"F3.wireOp",EDGE,"E16.5.8.0"),sQuery(id+"F3.wireOp",EDGE,"E16.8.8.0"),sQuery(id+"F3.wireOp",EDGE,"E16.14.8.0"),sQuery(id+"F3.wireOp",EDGE,"E16.18.8.0"),sQuery(id+"F3.wireOp",EDGE,"E16.23.8.0"),sQuery(id+"F3.wireOp",EDGE,"E16.29.8.0"),sQuery(id+"F3.wireOp",EDGE,"E16.32.8.0"),sQuery(id+"F3.wireOp",EDGE,"E16.36.8.0"),sQuery(id+"F3.wireOp",EDGE,"E16.40.8.0"),sQuery(id+"F3.wireOp",EDGE,"E16.43.8.0"),sQuery(id+"F3.wireOp",EDGE,"E16.46.8.0"),sQuery(id+"F3.wireOp",EDGE,"E16.50.8.0")])],"isStart":false});
            var Q15;
            Q15=makeQuery(id+"F4.opExtrude","CAP_FACE",FACE,{"disambiguationData":[OSD([sQuery(id+"F3.wireOp",EDGE,"E16.1.10.0"),sQuery(id+"F3.wireOp",EDGE,"E16.5.10.0"),sQuery(id+"F3.wireOp",EDGE,"E16.8.10.0"),sQuery(id+"F3.wireOp",EDGE,"E16.14.10.0"),sQuery(id+"F3.wireOp",EDGE,"E16.18.10.0"),sQuery(id+"F3.wireOp",EDGE,"E16.23.10.0"),sQuery(id+"F3.wireOp",EDGE,"E16.29.10.0"),sQuery(id+"F3.wireOp",EDGE,"E16.32.10.0"),sQuery(id+"F3.wireOp",EDGE,"E16.36.10.0"),sQuery(id+"F3.wireOp",EDGE,"E16.40.10.0"),sQuery(id+"F3.wireOp",EDGE,"E16.43.10.0"),sQuery(id+"F3.wireOp",EDGE,"E16.46.10.0"),sQuery(id+"F3.wireOp",EDGE,"E16.50.10.0")])],"isStart":false});
            var Q16;
            Q16=makeQuery(id+"F4.opExtrude","CAP_FACE",FACE,{"disambiguationData":[OSD([sQuery(id+"F3.wireOp",EDGE,"E16.1.11.0"),sQuery(id+"F3.wireOp",EDGE,"E16.5.11.0"),sQuery(id+"F3.wireOp",EDGE,"E16.8.11.0"),sQuery(id+"F3.wireOp",EDGE,"E16.14.11.0"),sQuery(id+"F3.wireOp",EDGE,"E16.18.11.0"),sQuery(id+"F3.wireOp",EDGE,"E16.23.11.0"),sQuery(id+"F3.wireOp",EDGE,"E16.29.11.0"),sQuery(id+"F3.wireOp",EDGE,"E16.32.11.0"),sQuery(id+"F3.wireOp",EDGE,"E16.36.11.0"),sQuery(id+"F3.wireOp",EDGE,"E16.40.11.0"),sQuery(id+"F3.wireOp",EDGE,"E16.43.11.0"),sQuery(id+"F3.wireOp",EDGE,"E16.46.11.0"),sQuery(id+"F3.wireOp",EDGE,"E16.50.11.0")])],"isStart":false});
            var Q17;
            Q17=makeQuery(id+"F4.opExtrude","CAP_FACE",FACE,{"disambiguationData":[OSD([sQuery(id+"F3.wireOp",EDGE,"E16.1.12.0"),sQuery(id+"F3.wireOp",EDGE,"E16.5.12.0"),sQuery(id+"F3.wireOp",EDGE,"E16.8.12.0"),sQuery(id+"F3.wireOp",EDGE,"E16.14.12.0"),sQuery(id+"F3.wireOp",EDGE,"E16.18.12.0"),sQuery(id+"F3.wireOp",EDGE,"E16.23.12.0"),sQuery(id+"F3.wireOp",EDGE,"E16.29.12.0"),sQuery(id+"F3.wireOp",EDGE,"E16.32.12.0"),sQuery(id+"F3.wireOp",EDGE,"E16.36.12.0"),sQuery(id+"F3.wireOp",EDGE,"E16.40.12.0"),sQuery(id+"F3.wireOp",EDGE,"E16.43.12.0"),sQuery(id+"F3.wireOp",EDGE,"E16.46.12.0"),sQuery(id+"F3.wireOp",EDGE,"E16.50.12.0")])],"isStart":false});
            var Q18;
            Q18=makeQuery(id+"F4.opExtrude","CAP_FACE",FACE,{"disambiguationData":[OSD([sQuery(id+"F3.wireOp",EDGE,"E16.1.15.0"),sQuery(id+"F3.wireOp",EDGE,"E16.5.15.0"),sQuery(id+"F3.wireOp",EDGE,"E16.8.15.0"),sQuery(id+"F3.wireOp",EDGE,"E16.14.15.0"),sQuery(id+"F3.wireOp",EDGE,"E16.18.15.0"),sQuery(id+"F3.wireOp",EDGE,"E16.23.15.0"),sQuery(id+"F3.wireOp",EDGE,"E16.29.15.0"),sQuery(id+"F3.wireOp",EDGE,"E16.32.15.0"),sQuery(id+"F3.wireOp",EDGE,"E16.36.15.0"),sQuery(id+"F3.wireOp",EDGE,"E16.40.15.0"),sQuery(id+"F3.wireOp",EDGE,"E16.43.15.0"),sQuery(id+"F3.wireOp",EDGE,"E16.46.15.0"),sQuery(id+"F3.wireOp",EDGE,"E16.50.15.0")])],"isStart":false});
            var Q19;
            Q19=makeQuery(id+"F4.opExtrude","CAP_FACE",FACE,{"disambiguationData":[OSD([sQuery(id+"F3.wireOp",EDGE,"E16.1.16.0"),sQuery(id+"F3.wireOp",EDGE,"E16.5.16.0"),sQuery(id+"F3.wireOp",EDGE,"E16.8.16.0"),sQuery(id+"F3.wireOp",EDGE,"E16.14.16.0"),sQuery(id+"F3.wireOp",EDGE,"E16.18.16.0"),sQuery(id+"F3.wireOp",EDGE,"E16.23.16.0"),sQuery(id+"F3.wireOp",EDGE,"E16.29.16.0"),sQuery(id+"F3.wireOp",EDGE,"E16.32.16.0"),sQuery(id+"F3.wireOp",EDGE,"E16.36.16.0"),sQuery(id+"F3.wireOp",EDGE,"E16.40.16.0"),sQuery(id+"F3.wireOp",EDGE,"E16.43.16.0"),sQuery(id+"F3.wireOp",EDGE,"E16.46.16.0"),sQuery(id+"F3.wireOp",EDGE,"E16.50.16.0")])],"isStart":false});
            var Q20;
            Q20=makeQuery(id+"F4.opExtrude","CAP_FACE",FACE,{"disambiguationData":[OSD([sQuery(id+"F3.wireOp",EDGE,"E16.1.13.0"),sQuery(id+"F3.wireOp",EDGE,"E16.5.13.0"),sQuery(id+"F3.wireOp",EDGE,"E16.8.13.0"),sQuery(id+"F3.wireOp",EDGE,"E16.14.13.0"),sQuery(id+"F3.wireOp",EDGE,"E16.18.13.0"),sQuery(id+"F3.wireOp",EDGE,"E16.23.13.0"),sQuery(id+"F3.wireOp",EDGE,"E16.29.13.0"),sQuery(id+"F3.wireOp",EDGE,"E16.32.13.0"),sQuery(id+"F3.wireOp",EDGE,"E16.36.13.0"),sQuery(id+"F3.wireOp",EDGE,"E16.40.13.0"),sQuery(id+"F3.wireOp",EDGE,"E16.43.13.0"),sQuery(id+"F3.wireOp",EDGE,"E16.46.13.0"),sQuery(id+"F3.wireOp",EDGE,"E16.50.13.0")])],"isStart":false});
            var Q21;
            Q21=makeQuery(id+"F4.opExtrude","CAP_FACE",FACE,{"disambiguationData":[OSD([sQuery(id+"F3.wireOp",EDGE,"E16.1.14.0"),sQuery(id+"F3.wireOp",EDGE,"E16.5.14.0"),sQuery(id+"F3.wireOp",EDGE,"E16.8.14.0"),sQuery(id+"F3.wireOp",EDGE,"E16.14.14.0"),sQuery(id+"F3.wireOp",EDGE,"E16.18.14.0"),sQuery(id+"F3.wireOp",EDGE,"E16.23.14.0"),sQuery(id+"F3.wireOp",EDGE,"E16.29.14.0"),sQuery(id+"F3.wireOp",EDGE,"E16.32.14.0"),sQuery(id+"F3.wireOp",EDGE,"E16.36.14.0"),sQuery(id+"F3.wireOp",EDGE,"E16.40.14.0"),sQuery(id+"F3.wireOp",EDGE,"E16.43.14.0"),sQuery(id+"F3.wireOp",EDGE,"E16.46.14.0"),sQuery(id+"F3.wireOp",EDGE,"E16.50.14.0")])],"isStart":false});
            var Q22;
            Q22=makeQuery(id+"F4.opExtrude","CAP_FACE",FACE,{"disambiguationData":[OSD([sQuery(id+"F3.wireOp",EDGE,"E16.1.17.0"),sQuery(id+"F3.wireOp",EDGE,"E16.5.17.0"),sQuery(id+"F3.wireOp",EDGE,"E16.8.17.0"),sQuery(id+"F3.wireOp",EDGE,"E16.14.17.0"),sQuery(id+"F3.wireOp",EDGE,"E16.18.17.0"),sQuery(id+"F3.wireOp",EDGE,"E16.23.17.0"),sQuery(id+"F3.wireOp",EDGE,"E16.29.17.0"),sQuery(id+"F3.wireOp",EDGE,"E16.32.17.0"),sQuery(id+"F3.wireOp",EDGE,"E16.36.17.0"),sQuery(id+"F3.wireOp",EDGE,"E16.40.17.0"),sQuery(id+"F3.wireOp",EDGE,"E16.43.17.0"),sQuery(id+"F3.wireOp",EDGE,"E16.46.17.0"),sQuery(id+"F3.wireOp",EDGE,"E16.50.17.0")])],"isStart":false});
            var Q23;
            Q23=makeQuery(id+"F4.opExtrude","CAP_FACE",FACE,{"disambiguationData":[OSD([sQuery(id+"F3.wireOp",EDGE,"E16.1.18.0"),sQuery(id+"F3.wireOp",EDGE,"E16.5.18.0"),sQuery(id+"F3.wireOp",EDGE,"E16.8.18.0"),sQuery(id+"F3.wireOp",EDGE,"E16.14.18.0"),sQuery(id+"F3.wireOp",EDGE,"E16.18.18.0"),sQuery(id+"F3.wireOp",EDGE,"E16.23.18.0"),sQuery(id+"F3.wireOp",EDGE,"E16.29.18.0"),sQuery(id+"F3.wireOp",EDGE,"E16.32.18.0"),sQuery(id+"F3.wireOp",EDGE,"E16.36.18.0"),sQuery(id+"F3.wireOp",EDGE,"E16.40.18.0"),sQuery(id+"F3.wireOp",EDGE,"E16.43.18.0"),sQuery(id+"F3.wireOp",EDGE,"E16.46.18.0"),sQuery(id+"F3.wireOp",EDGE,"E16.50.18.0")])],"isStart":false});
            var Q24;
            Q24=makeQuery(id+"F4.opExtrude","CAP_FACE",FACE,{"disambiguationData":[OSD([sQuery(id+"F3.wireOp",EDGE,"E16.1.24.0"),sQuery(id+"F3.wireOp",EDGE,"E16.5.24.0"),sQuery(id+"F3.wireOp",EDGE,"E16.8.24.0"),sQuery(id+"F3.wireOp",EDGE,"E16.14.24.0"),sQuery(id+"F3.wireOp",EDGE,"E16.18.24.0"),sQuery(id+"F3.wireOp",EDGE,"E16.23.24.0"),sQuery(id+"F3.wireOp",EDGE,"E16.29.24.0"),sQuery(id+"F3.wireOp",EDGE,"E16.32.24.0"),sQuery(id+"F3.wireOp",EDGE,"E16.36.24.0"),sQuery(id+"F3.wireOp",EDGE,"E16.40.24.0"),sQuery(id+"F3.wireOp",EDGE,"E16.43.24.0"),sQuery(id+"F3.wireOp",EDGE,"E16.46.24.0"),sQuery(id+"F3.wireOp",EDGE,"E16.50.24.0")])],"isStart":false});
            var Q25;
            Q25=makeQuery(id+"F4.opExtrude","CAP_FACE",FACE,{"disambiguationData":[OSD([sQuery(id+"F3.wireOp",EDGE,"E16.1.23.0"),sQuery(id+"F3.wireOp",EDGE,"E16.5.23.0"),sQuery(id+"F3.wireOp",EDGE,"E16.8.23.0"),sQuery(id+"F3.wireOp",EDGE,"E16.14.23.0"),sQuery(id+"F3.wireOp",EDGE,"E16.18.23.0"),sQuery(id+"F3.wireOp",EDGE,"E16.23.23.0"),sQuery(id+"F3.wireOp",EDGE,"E16.29.23.0"),sQuery(id+"F3.wireOp",EDGE,"E16.32.23.0"),sQuery(id+"F3.wireOp",EDGE,"E16.36.23.0"),sQuery(id+"F3.wireOp",EDGE,"E16.40.23.0"),sQuery(id+"F3.wireOp",EDGE,"E16.43.23.0"),sQuery(id+"F3.wireOp",EDGE,"E16.46.23.0"),sQuery(id+"F3.wireOp",EDGE,"E16.50.23.0")])],"isStart":false});
            var Q26;
            Q26=makeQuery(id+"F4.opExtrude","CAP_FACE",FACE,{"disambiguationData":[OSD([sQuery(id+"F3.wireOp",EDGE,"E16.1.22.0"),sQuery(id+"F3.wireOp",EDGE,"E16.5.22.0"),sQuery(id+"F3.wireOp",EDGE,"E16.8.22.0"),sQuery(id+"F3.wireOp",EDGE,"E16.14.22.0"),sQuery(id+"F3.wireOp",EDGE,"E16.18.22.0"),sQuery(id+"F3.wireOp",EDGE,"E16.23.22.0"),sQuery(id+"F3.wireOp",EDGE,"E16.29.22.0"),sQuery(id+"F3.wireOp",EDGE,"E16.32.22.0"),sQuery(id+"F3.wireOp",EDGE,"E16.36.22.0"),sQuery(id+"F3.wireOp",EDGE,"E16.40.22.0"),sQuery(id+"F3.wireOp",EDGE,"E16.43.22.0"),sQuery(id+"F3.wireOp",EDGE,"E16.46.22.0"),sQuery(id+"F3.wireOp",EDGE,"E16.50.22.0")])],"isStart":false});
            var Q27;
            Q27=makeQuery(id+"F4.opExtrude","CAP_FACE",FACE,{"disambiguationData":[OSD([sQuery(id+"F3.wireOp",EDGE,"E16.1.21.0"),sQuery(id+"F3.wireOp",EDGE,"E16.5.21.0"),sQuery(id+"F3.wireOp",EDGE,"E16.8.21.0"),sQuery(id+"F3.wireOp",EDGE,"E16.14.21.0"),sQuery(id+"F3.wireOp",EDGE,"E16.18.21.0"),sQuery(id+"F3.wireOp",EDGE,"E16.23.21.0"),sQuery(id+"F3.wireOp",EDGE,"E16.29.21.0"),sQuery(id+"F3.wireOp",EDGE,"E16.32.21.0"),sQuery(id+"F3.wireOp",EDGE,"E16.36.21.0"),sQuery(id+"F3.wireOp",EDGE,"E16.40.21.0"),sQuery(id+"F3.wireOp",EDGE,"E16.43.21.0"),sQuery(id+"F3.wireOp",EDGE,"E16.46.21.0"),sQuery(id+"F3.wireOp",EDGE,"E16.50.21.0")])],"isStart":false});
            var Q28;
            Q28=makeQuery(id+"F4.opExtrude","CAP_FACE",FACE,{"disambiguationData":[OSD([sQuery(id+"F3.wireOp",EDGE,"E16.1.20.0"),sQuery(id+"F3.wireOp",EDGE,"E16.5.20.0"),sQuery(id+"F3.wireOp",EDGE,"E16.8.20.0"),sQuery(id+"F3.wireOp",EDGE,"E16.14.20.0"),sQuery(id+"F3.wireOp",EDGE,"E16.18.20.0"),sQuery(id+"F3.wireOp",EDGE,"E16.23.20.0"),sQuery(id+"F3.wireOp",EDGE,"E16.29.20.0"),sQuery(id+"F3.wireOp",EDGE,"E16.32.20.0"),sQuery(id+"F3.wireOp",EDGE,"E16.36.20.0"),sQuery(id+"F3.wireOp",EDGE,"E16.40.20.0"),sQuery(id+"F3.wireOp",EDGE,"E16.43.20.0"),sQuery(id+"F3.wireOp",EDGE,"E16.46.20.0"),sQuery(id+"F3.wireOp",EDGE,"E16.50.20.0")])],"isStart":false});
            var Q29;
            Q29=makeQuery(id+"F4.opExtrude","CAP_FACE",FACE,{"disambiguationData":[OSD([sQuery(id+"F3.wireOp",EDGE,"E16.1.19.0"),sQuery(id+"F3.wireOp",EDGE,"E16.5.19.0"),sQuery(id+"F3.wireOp",EDGE,"E16.8.19.0"),sQuery(id+"F3.wireOp",EDGE,"E16.14.19.0"),sQuery(id+"F3.wireOp",EDGE,"E16.18.19.0"),sQuery(id+"F3.wireOp",EDGE,"E16.23.19.0"),sQuery(id+"F3.wireOp",EDGE,"E16.29.19.0"),sQuery(id+"F3.wireOp",EDGE,"E16.32.19.0"),sQuery(id+"F3.wireOp",EDGE,"E16.36.19.0"),sQuery(id+"F3.wireOp",EDGE,"E16.40.19.0"),sQuery(id+"F3.wireOp",EDGE,"E16.43.19.0"),sQuery(id+"F3.wireOp",EDGE,"E16.46.19.0"),sQuery(id+"F3.wireOp",EDGE,"E16.50.19.0")])],"isStart":false});
            extrude(context, id + "F5", {"entities" : qUnion([Q0, Q1, Q2, Q3, Q4, Q5, Q6, Q7, Q8, Q9, Q10, Q11, Q12, Q13, Q14, Q15, Q16, Q17, Q18, Q19, Q20, Q21, Q22, Q23, Q24, Q25, Q26, Q27, Q28, Q29]), "operationType" : NewBodyOperationType.ADD, "depth" : 57.15 * mm});
        }
        {
            var Q0;
            Q0=makeQuery(id+"F4.boolean.opBoolean","MERGE",FACE,{"derivedFrom":[makeQuery(id+"F1.opExtrude","CAP_FACE",FACE,{"disambiguationData":[OSD([sQuery(id+"F0.wireOp",EDGE,"E0")])],"isStart":false}),makeQuery(id+"F4.opExtrude","CAP_FACE",FACE,{"disambiguationData":[OSD([sQuery(id+"F3.wireOp",EDGE,"E1.trimOffspring"),sQuery(id+"F3.wireOp",EDGE,"E2"),sQuery(id+"F3.wireOp",EDGE,"E3"),sQuery(id+"F3.wireOp",EDGE,"E4.MirrorCS"),sQuery(id+"F3.wireOp",EDGE,"E5.MirrorCS"),sQuery(id+"F3.wireOp",EDGE,"E7.filletArc"),sQuery(id+"F3.wireOp",EDGE,"E8"),sQuery(id+"F3.wireOp",EDGE,"E9.MirrorCS"),sQuery(id+"F3.wireOp",EDGE,"E10.MirrorCS"),sQuery(id+"F3.wireOp",EDGE,"E11.filletArc"),sQuery(id+"F3.wireOp",EDGE,"E12.filletArc"),sQuery(id+"F3.wireOp",EDGE,"E13.filletArc"),sQuery(id+"F3.wireOp",EDGE,"E14.filletArc")])],"isStart":true})]});
            var sketch = newSketch(context, id + "F6", { "sketchPlane" : qUnion([Q0])});
            skPoint(sketch, "E17", {"position": v(0, 0) * mm});
            skSolve(sketch);
        }
        {
            var Q0;
            {var subQ144=sQuery(id+"F3.wireOp",EDGE,"E1.trimOffspring");Q0=makeQuery(id+"F6.imprint","IMPRINT",FACE,{"disambiguationData":[TD([[makeQuery(id+"F6.imprint","IMPRINT",EDGE,{"derivedFrom":makeQuery(id+"F4.opExtrude","CAP_EDGE",EDGE,{"disambiguationData":[OSD([subQ144])],"isStart":true})}),1.0]])]});}
            var sketch = newSketch(context, id + "F7", { "sketchPlane" : qUnion([Q0])});
            skCircle(sketch, "E18", {"center": v(0, 0) * mm, "radius": 12.7 * mm});
            skSolve(sketch);
        }
        {
            var Q0;
            Q0 = qSketchRegion(id + "F7", true);
            extrude(context, id + "F8", {"entities" : qUnion([Q0]), "operationType" : NewBodyOperationType.ADD, "depth" : 12.7 * mm});
        }
        {
            var Q0;
            Q0=makeQuery(id+"F8.opExtrude","CAP_FACE",FACE,{"disambiguationData":[OSD([sQuery(id+"F7.wireOp",EDGE,"E18")])],"isStart":false});
            var sketch = newSketch(context, id + "F9", { "sketchPlane" : qUnion([Q0])});
            skCircle(sketch, "E19", {"center": v(0, 0) * mm, "radius": 6.35 * mm});
            skSolve(sketch);
        }
        {
            var Q0;
            Q0=makeQuery(id+"F9.imprint","IMPRINT",FACE,{"disambiguationData":[TD([[makeQuery(id+"F9.imprint","IMPRINT",EDGE,{"derivedFrom":sQuery(id+"F9.wireOp",EDGE,"E19")}),1.0]])]});
            extrude(context, id + "F10", {"entities" : qUnion([Q0]), "operationType" : NewBodyOperationType.REMOVE, "oppositeDirection" : true, "depth" : 127 * mm});
        }
    });
